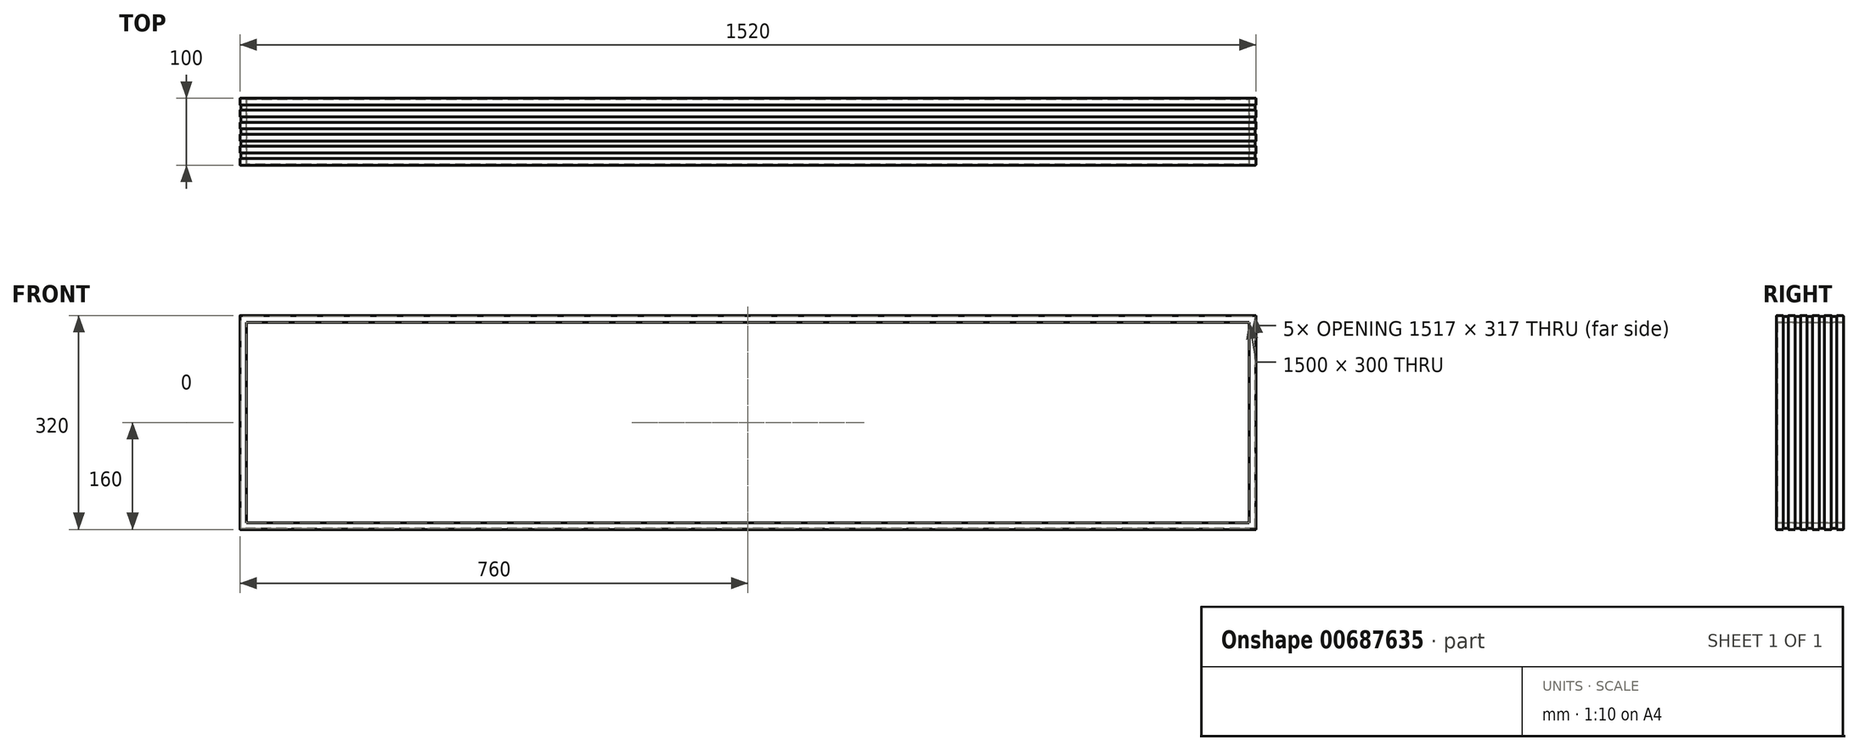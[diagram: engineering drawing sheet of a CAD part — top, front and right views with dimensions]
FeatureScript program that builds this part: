
annotation { "Feature Type Name" : "Feature", "Feature Type Description" : "" }
export const myFeature = defineFeature(function(context is Context, id is Id, definition is map)
    precondition{}
    {
        {
            var Q0;
            Q0=qCreatedBy(makeId("Front.planeOp"),FACE);
            var sketch = newSketch(context, id + "F0", { "sketchPlane" : qUnion([Q0])});
            skLineSegment(sketch, "E0.bottom", {"start": v(-1550, 0) * mm, "end": v(-1500, 0) * mm});
            skLineSegment(sketch, "E0.top", {"start": v(-1550, -2720) * mm, "end": v(-1500, -2720) * mm});
            skLineSegment(sketch, "E0.left", {"start": v(-1550, 0) * mm, "end": v(-1550, -2720) * mm});
            skLineSegment(sketch, "E0.right", {"start": v(-1500, 0) * mm, "end": v(-1500, -2720) * mm});
            skLineSegment(sketch, "E1.MirrorCS", {"start": v(1550, -2720) * mm, "end": v(1500, -2720) * mm});
            skLineSegment(sketch, "E2.MirrorCS", {"start": v(1500, 0) * mm, "end": v(1500, -2720) * mm});
            skLineSegment(sketch, "E3.MirrorCS", {"start": v(1550, 0) * mm, "end": v(1500, 0) * mm});
            skLineSegment(sketch, "E4.MirrorCS", {"start": v(1550, 0) * mm, "end": v(1550, -2720) * mm});
            skSolve(sketch);
        }
        {
            var Q0;
            Q0=qSketchRegion(id+"F0",true);
            extrude(context, id + "F1", {"entities" : qUnion([Q0]), "depth" : 100 * mm, "offsetDistance" : 25 * mm});
        }
        {
            var Q0;
            Q0=makeQuery(id+"F1.opExtrude","SWEPT_FACE",FACE,{"disambiguationData":[OSD([sQuery(id+"F0.wireOp",EDGE,"E0.bottom")])]});
            var sketch = newSketch(context, id + "F2", { "sketchPlane" : qUnion([Q0])});
            skLineSegment(sketch, "E5.bottom", {"start": v(-1550, -100) * mm, "end": v(-3070, -100) * mm});
            skLineSegment(sketch, "E5.top", {"start": v(-1550, 0) * mm, "end": v(-3070, 0) * mm});
            skLineSegment(sketch, "E5.left", {"start": v(-1550, -100) * mm, "end": v(-1550, 0) * mm});
            skLineSegment(sketch, "E5.right", {"start": v(-3070, -100) * mm, "end": v(-3070, 0) * mm});
            skLineSegment(sketch, "E6.bottom", {"start": v(-1500, -100) * mm, "end": v(1500, -100) * mm});
            skLineSegment(sketch, "E6.top", {"start": v(-1500, 0) * mm, "end": v(1500, 0) * mm});
            skLineSegment(sketch, "E6.left", {"start": v(-1500, -100) * mm, "end": v(-1500, 0) * mm});
            skLineSegment(sketch, "E6.right", {"start": v(1500, -100) * mm, "end": v(1500, 0) * mm});
            skLineSegment(sketch, "E7.bottom", {"start": v(1550, -100) * mm, "end": v(2770, -100) * mm});
            skLineSegment(sketch, "E7.top", {"start": v(1550, 0) * mm, "end": v(2770, 0) * mm});
            skLineSegment(sketch, "E7.left", {"start": v(1550, -100) * mm, "end": v(1550, 0) * mm});
            skLineSegment(sketch, "E7.right", {"start": v(2770, -100) * mm, "end": v(2770, 0) * mm});
            skSolve(sketch);
        }
        {
            var Q0;
            Q0=qSketchRegion(id+"F2",true);
            extrude(context, id + "F3", {"entities" : qUnion([Q0]), "oppositeDirection" : true, "depth" : 320 * mm, "offsetDistance" : 25 * mm});
        }
        {
            var Q0;
            Q0=makeQuery(id+"F3.opExtrude","SWEPT_FACE",FACE,{"disambiguationData":[OSD([sQuery(id+"F2.wireOp",EDGE,"E6.bottom")])]});
            var sketch = newSketch(context, id + "F4", { "sketchPlane" : qUnion([Q0])});
            skLineSegment(sketch, "E8.0", {"start": v(-1560, -10) * mm, "end": v(-3060, -10) * mm});
            skLineSegment(sketch, "E8.1", {"start": v(-1560, -310) * mm, "end": v(-1560, -10) * mm});
            skLineSegment(sketch, "E8.2", {"start": v(-3060, -310) * mm, "end": v(-1560, -310) * mm});
            skLineSegment(sketch, "E8.3", {"start": v(-3060, -10) * mm, "end": v(-3060, -310) * mm});
            skLineSegment(sketch, "E9.0", {"start": v(1490, -10) * mm, "end": v(-1490, -10) * mm});
            skLineSegment(sketch, "E9.1", {"start": v(1490, -310) * mm, "end": v(1490, -10) * mm});
            skLineSegment(sketch, "E9.2", {"start": v(-1490, -310) * mm, "end": v(1490, -310) * mm});
            skLineSegment(sketch, "E9.3", {"start": v(-1490, -10) * mm, "end": v(-1490, -310) * mm});
            skLineSegment(sketch, "E10.0", {"start": v(2760, -10) * mm, "end": v(1560, -10) * mm});
            skLineSegment(sketch, "E10.1", {"start": v(2760, -310) * mm, "end": v(2760, -10) * mm});
            skLineSegment(sketch, "E10.2", {"start": v(1560, -310) * mm, "end": v(2760, -310) * mm});
            skLineSegment(sketch, "E10.3", {"start": v(1560, -10) * mm, "end": v(1560, -310) * mm});
            skSolve(sketch);
        }
        {
            var Q0;
            Q0=qSketchRegion(id+"F4",true);
            extrude(context, id + "F5", {"entities" : qUnion([Q0]), "operationType" : NewBodyOperationType.REMOVE, "endBound" : BoundingType.THROUGH_ALL, "oppositeDirection" : true, "depth" : 25 * mm, "offsetDistance" : 25 * mm});
        }
        {
            var Q0;
            Q0=makeQuery(id+"F3.opExtrude","SWEPT_FACE",FACE,{"disambiguationData":[OSD([sQuery(id+"F2.wireOp",EDGE,"E5.right")])]});
            var sketch = newSketch(context, id + "F6", { "sketchPlane" : qUnion([Q0])});
            skLineSegment(sketch, "E11", {"start": v(10, 0) * mm, "end": v(10, -1.5) * mm});
            skLineSegment(sketch, "E12", {"start": v(10, -1.5) * mm, "end": v(18, -1.5) * mm});
            skLineSegment(sketch, "E13", {"start": v(18, -1.5) * mm, "end": v(18, 0) * mm});
            skLineSegment(sketch, "E14.1.0.0", {"start": v(36, -1.5) * mm, "end": v(36, 0) * mm});
            skLineSegment(sketch, "E14.1.0.1", {"start": v(28, -1.5) * mm, "end": v(36, -1.5) * mm});
            skLineSegment(sketch, "E14.1.0.2", {"start": v(28, 0) * mm, "end": v(28, -1.5) * mm});
            skLineSegment(sketch, "E14.2.0.0", {"start": v(54, -1.5) * mm, "end": v(54, 0) * mm});
            skLineSegment(sketch, "E14.2.0.1", {"start": v(46, -1.5) * mm, "end": v(54, -1.5) * mm});
            skLineSegment(sketch, "E14.2.0.2", {"start": v(46, 0) * mm, "end": v(46, -1.5) * mm});
            skLineSegment(sketch, "E14.3.0.0", {"start": v(72, -1.5) * mm, "end": v(72, 0) * mm});
            skLineSegment(sketch, "E14.3.0.1", {"start": v(64, -1.5) * mm, "end": v(72, -1.5) * mm});
            skLineSegment(sketch, "E14.3.0.2", {"start": v(64, 0) * mm, "end": v(64, -1.5) * mm});
            skLineSegment(sketch, "E14.4.0.0", {"start": v(90, -1.5) * mm, "end": v(90, 0) * mm});
            skLineSegment(sketch, "E14.4.0.1", {"start": v(82, -1.5) * mm, "end": v(90, -1.5) * mm});
            skLineSegment(sketch, "E14.4.0.2", {"start": v(82, 0) * mm, "end": v(82, -1.5) * mm});
            skLineSegment(sketch, "E14.direction1", {"start": v(10, -1.5) * mm, "end": v(28, -1.5) * mm, "construction": true});
            skLineSegment(sketch, "E15", {"start": v(10, 0) * mm, "end": v(18, 0) * mm});
            skLineSegment(sketch, "E16", {"start": v(28, 0) * mm, "end": v(36, 0) * mm});
            skLineSegment(sketch, "E17", {"start": v(46, 0) * mm, "end": v(54, 0) * mm});
            skLineSegment(sketch, "E18", {"start": v(64, 0) * mm, "end": v(72, 0) * mm});
            skLineSegment(sketch, "E19", {"start": v(82, 0) * mm, "end": v(90, 0) * mm});
            skLineSegment(sketch, "E20", {"start": v(100, -160) * mm, "end": v(0, -160) * mm, "construction": true});
            skLineSegment(sketch, "E21.MirrorCS", {"start": v(90, -318.5) * mm, "end": v(90, -320) * mm});
            skLineSegment(sketch, "E22.MirrorCS", {"start": v(64, -320) * mm, "end": v(64, -318.5) * mm});
            skLineSegment(sketch, "E23.MirrorCS", {"start": v(10, -320) * mm, "end": v(10, -318.5) * mm});
            skLineSegment(sketch, "E24.MirrorCS", {"start": v(18, -318.5) * mm, "end": v(18, -320) * mm});
            skLineSegment(sketch, "E25.MirrorCS", {"start": v(36, -318.5) * mm, "end": v(36, -320) * mm});
            skLineSegment(sketch, "E26.MirrorCS", {"start": v(28, -320) * mm, "end": v(28, -318.5) * mm});
            skLineSegment(sketch, "E27.MirrorCS", {"start": v(54, -318.5) * mm, "end": v(54, -320) * mm});
            skLineSegment(sketch, "E28.MirrorCS", {"start": v(46, -320) * mm, "end": v(46, -318.5) * mm});
            skLineSegment(sketch, "E29.MirrorCS", {"start": v(72, -318.5) * mm, "end": v(72, -320) * mm});
            skLineSegment(sketch, "E30.MirrorCS", {"start": v(82, -320) * mm, "end": v(82, -318.5) * mm});
            skLineSegment(sketch, "E31.MirrorCS", {"start": v(10, -320) * mm, "end": v(18, -320) * mm});
            skLineSegment(sketch, "E32.MirrorCS", {"start": v(10, -318.5) * mm, "end": v(18, -318.5) * mm});
            skLineSegment(sketch, "E33.MirrorCS", {"start": v(64, -318.5) * mm, "end": v(72, -318.5) * mm});
            skLineSegment(sketch, "E34.MirrorCS", {"start": v(64, -320) * mm, "end": v(72, -320) * mm});
            skLineSegment(sketch, "E35.MirrorCS", {"start": v(82, -320) * mm, "end": v(90, -320) * mm});
            skLineSegment(sketch, "E36.MirrorCS", {"start": v(28, -320) * mm, "end": v(36, -320) * mm});
            skLineSegment(sketch, "E37.MirrorCS", {"start": v(82, -318.5) * mm, "end": v(90, -318.5) * mm});
            skLineSegment(sketch, "E38.MirrorCS", {"start": v(10, -318.5) * mm, "end": v(28, -318.5) * mm, "construction": true});
            skLineSegment(sketch, "E39.MirrorCS", {"start": v(46, -320) * mm, "end": v(54, -320) * mm});
            skLineSegment(sketch, "E40.MirrorCS", {"start": v(28, -318.5) * mm, "end": v(36, -318.5) * mm});
            skLineSegment(sketch, "E41.MirrorCS", {"start": v(46, -318.5) * mm, "end": v(54, -318.5) * mm});
            skSolve(sketch);
        }
        {
            var Q0;
            Q0=qSketchRegion(id+"F6",true);
            extrude(context, id + "F7", {"entities" : qUnion([Q0]), "operationType" : NewBodyOperationType.REMOVE, "endBound" : BoundingType.THROUGH_ALL, "oppositeDirection" : true, "depth" : 25 * mm, "offsetDistance" : 25 * mm});
        }
        {
            var Q0;
            {var subQ0=sQuery(id+"F2.wireOp",EDGE,"E5.top");var subQ1=sQuery(id+"F2.wireOp",EDGE,"E5.left");var subQ2=sQuery(id+"F2.wireOp",EDGE,"E5.right");Q0=makeQuery(id+"F7.boolean.opBoolean","SPLIT",FACE,{"disambiguationData":[TD([makeQuery(id+"F3.opExtrude","SWEPT_FACE",FACE,{"disambiguationData":[OSD([subQ0])]})])],"derivedFrom":makeQuery(id+"F3.opExtrude","CAP_FACE",FACE,{"disambiguationData":[OSD([sQuery(id+"F2.wireOp",EDGE,"E5.bottom"),subQ0,subQ1,subQ2])],"isStart":true})});}
            var sketch = newSketch(context, id + "F8", { "sketchPlane" : qUnion([Q0])});
            skLineSegment(sketch, "E42.bottom", {"start": v(-3068.5, -90) * mm, "end": v(-3070, -90) * mm});
            skLineSegment(sketch, "E42.top", {"start": v(-3068.5, -82) * mm, "end": v(-3070, -82) * mm});
            skLineSegment(sketch, "E42.left", {"start": v(-3068.5, -90) * mm, "end": v(-3068.5, -82) * mm});
            skLineSegment(sketch, "E42.right", {"start": v(-3070, -90) * mm, "end": v(-3070, -82) * mm});
            skLineSegment(sketch, "E43.0.1.0", {"start": v(-3068.5, -64) * mm, "end": v(-3070, -64) * mm});
            skLineSegment(sketch, "E43.0.1.1", {"start": v(-3068.5, -72) * mm, "end": v(-3070, -72) * mm});
            skLineSegment(sketch, "E43.0.1.2", {"start": v(-3070, -72) * mm, "end": v(-3070, -64) * mm});
            skLineSegment(sketch, "E43.0.1.3", {"start": v(-3068.5, -72) * mm, "end": v(-3068.5, -64) * mm});
            skLineSegment(sketch, "E43.0.2.0", {"start": v(-3068.5, -46) * mm, "end": v(-3070, -46) * mm});
            skLineSegment(sketch, "E43.0.2.1", {"start": v(-3068.5, -54) * mm, "end": v(-3070, -54) * mm});
            skLineSegment(sketch, "E43.0.2.2", {"start": v(-3070, -54) * mm, "end": v(-3070, -46) * mm});
            skLineSegment(sketch, "E43.0.2.3", {"start": v(-3068.5, -54) * mm, "end": v(-3068.5, -46) * mm});
            skLineSegment(sketch, "E43.0.3.0", {"start": v(-3068.5, -28) * mm, "end": v(-3070, -28) * mm});
            skLineSegment(sketch, "E43.0.3.1", {"start": v(-3068.5, -36) * mm, "end": v(-3070, -36) * mm});
            skLineSegment(sketch, "E43.0.3.2", {"start": v(-3070, -36) * mm, "end": v(-3070, -28) * mm});
            skLineSegment(sketch, "E43.0.3.3", {"start": v(-3068.5, -36) * mm, "end": v(-3068.5, -28) * mm});
            skLineSegment(sketch, "E43.0.4.0", {"start": v(-3068.5, -10) * mm, "end": v(-3070, -10) * mm});
            skLineSegment(sketch, "E43.0.4.1", {"start": v(-3068.5, -18) * mm, "end": v(-3070, -18) * mm});
            skLineSegment(sketch, "E43.0.4.2", {"start": v(-3070, -18) * mm, "end": v(-3070, -10) * mm});
            skLineSegment(sketch, "E43.0.4.3", {"start": v(-3068.5, -18) * mm, "end": v(-3068.5, -10) * mm});
            skLineSegment(sketch, "E43.direction1", {"start": v(-3070, -90) * mm, "end": v(-2770, -90) * mm, "construction": true});
            skLineSegment(sketch, "E43.direction2", {"start": v(-3070, -90) * mm, "end": v(-3070, -72) * mm, "construction": true});
            skPoint(sketch, "E44.0", {"position": v(0, -10) * mm});
            skLineSegment(sketch, "E45.MirrorCS", {"start": v(3068.5, -64) * mm, "end": v(3070, -64) * mm});
            skLineSegment(sketch, "E46.MirrorCS", {"start": v(3068.5, -36) * mm, "end": v(3070, -36) * mm});
            skLineSegment(sketch, "E47.MirrorCS", {"start": v(3068.5, -90) * mm, "end": v(3070, -90) * mm});
            skLineSegment(sketch, "E48.MirrorCS", {"start": v(3068.5, -82) * mm, "end": v(3070, -82) * mm});
            skLineSegment(sketch, "E49.MirrorCS", {"start": v(3068.5, -72) * mm, "end": v(3070, -72) * mm});
            skLineSegment(sketch, "E50.MirrorCS", {"start": v(3068.5, -46) * mm, "end": v(3070, -46) * mm});
            skLineSegment(sketch, "E51.MirrorCS", {"start": v(3068.5, -54) * mm, "end": v(3070, -54) * mm});
            skLineSegment(sketch, "E52.MirrorCS", {"start": v(3070, -36) * mm, "end": v(3070, -28) * mm});
            skLineSegment(sketch, "E53.MirrorCS", {"start": v(3068.5, -90) * mm, "end": v(3068.5, -82) * mm});
            skLineSegment(sketch, "E54.MirrorCS", {"start": v(3070, -72) * mm, "end": v(3070, -64) * mm});
            skLineSegment(sketch, "E55.MirrorCS", {"start": v(3070, -54) * mm, "end": v(3070, -46) * mm});
            skLineSegment(sketch, "E56.MirrorCS", {"start": v(3068.5, -36) * mm, "end": v(3068.5, -28) * mm});
            skLineSegment(sketch, "E57.MirrorCS", {"start": v(3070, -90) * mm, "end": v(3070, -82) * mm});
            skLineSegment(sketch, "E58.MirrorCS", {"start": v(3068.5, -72) * mm, "end": v(3068.5, -64) * mm});
            skLineSegment(sketch, "E59.MirrorCS", {"start": v(3068.5, -54) * mm, "end": v(3068.5, -46) * mm});
            skLineSegment(sketch, "E60.MirrorCS", {"start": v(3068.5, -28) * mm, "end": v(3070, -28) * mm});
            skLineSegment(sketch, "E61.MirrorCS", {"start": v(3070, -90) * mm, "end": v(3070, -72) * mm, "construction": true});
            skLineSegment(sketch, "E62.MirrorCS", {"start": v(3070, -90) * mm, "end": v(2770, -90) * mm, "construction": true});
            skLineSegment(sketch, "E63.MirrorCS", {"start": v(3068.5, -18) * mm, "end": v(3070, -18) * mm});
            skLineSegment(sketch, "E64.MirrorCS", {"start": v(3070, -18) * mm, "end": v(3070, -10) * mm});
            skLineSegment(sketch, "E65.MirrorCS", {"start": v(3068.5, -18) * mm, "end": v(3068.5, -10) * mm});
            skLineSegment(sketch, "E66.MirrorCS", {"start": v(3068.5, -10) * mm, "end": v(3070, -10) * mm});
            skLineSegment(sketch, "E67", {"start": v(-2310, 0) * mm, "end": v(-2310, -98.65) * mm, "construction": true});
            skLineSegment(sketch, "E68.MirrorCS", {"start": v(-1551.5, -90) * mm, "end": v(-1550, -90) * mm});
            skLineSegment(sketch, "E69.MirrorCS", {"start": v(-1551.5, -72) * mm, "end": v(-1550, -72) * mm});
            skLineSegment(sketch, "E70.MirrorCS", {"start": v(-1551.5, -46) * mm, "end": v(-1550, -46) * mm});
            skLineSegment(sketch, "E71.MirrorCS", {"start": v(-1551.5, -28) * mm, "end": v(-1550, -28) * mm});
            skLineSegment(sketch, "E72.MirrorCS", {"start": v(-1551.5, -36) * mm, "end": v(-1550, -36) * mm});
            skLineSegment(sketch, "E73.MirrorCS", {"start": v(-1551.5, -10) * mm, "end": v(-1550, -10) * mm});
            skLineSegment(sketch, "E74.MirrorCS", {"start": v(-1551.5, -64) * mm, "end": v(-1550, -64) * mm});
            skLineSegment(sketch, "E75.MirrorCS", {"start": v(-1551.5, -54) * mm, "end": v(-1550, -54) * mm});
            skLineSegment(sketch, "E76.MirrorCS", {"start": v(-1551.5, -18) * mm, "end": v(-1550, -18) * mm});
            skLineSegment(sketch, "E77.MirrorCS", {"start": v(-1551.5, -82) * mm, "end": v(-1550, -82) * mm});
            skLineSegment(sketch, "E78.MirrorCS", {"start": v(-1550, -90) * mm, "end": v(-1550, -82) * mm});
            skLineSegment(sketch, "E79.MirrorCS", {"start": v(-1550, -72) * mm, "end": v(-1550, -64) * mm});
            skLineSegment(sketch, "E80.MirrorCS", {"start": v(-1551.5, -72) * mm, "end": v(-1551.5, -64) * mm});
            skLineSegment(sketch, "E81.MirrorCS", {"start": v(-1551.5, -36) * mm, "end": v(-1551.5, -28) * mm});
            skLineSegment(sketch, "E82.MirrorCS", {"start": v(-1550, -90) * mm, "end": v(-1550, -72) * mm, "construction": true});
            skLineSegment(sketch, "E83.MirrorCS", {"start": v(-1550, -18) * mm, "end": v(-1550, -10) * mm});
            skLineSegment(sketch, "E84.MirrorCS", {"start": v(-1550, -90) * mm, "end": v(-1850, -90) * mm, "construction": true});
            skLineSegment(sketch, "E85.MirrorCS", {"start": v(-1550, -54) * mm, "end": v(-1550, -46) * mm});
            skLineSegment(sketch, "E86.MirrorCS", {"start": v(-1551.5, -54) * mm, "end": v(-1551.5, -46) * mm});
            skLineSegment(sketch, "E87.MirrorCS", {"start": v(-1551.5, -90) * mm, "end": v(-1551.5, -82) * mm});
            skLineSegment(sketch, "E88.MirrorCS", {"start": v(-1550, -36) * mm, "end": v(-1550, -28) * mm});
            skLineSegment(sketch, "E89.MirrorCS", {"start": v(-1551.5, -18) * mm, "end": v(-1551.5, -10) * mm});
            skSolve(sketch);
        }
        {
            var Q0;
            Q0=qSketchRegion(id+"F8",true);
            extrude(context, id + "F9", {"entities" : qUnion([Q0]), "operationType" : NewBodyOperationType.REMOVE, "endBound" : BoundingType.THROUGH_ALL, "oppositeDirection" : true, "depth" : 25 * mm, "offsetDistance" : 25 * mm});
        }
        {
            var Q0;
            Q0=makeQuery(id+"F3.opExtrude","SWEPT_FACE",FACE,{"disambiguationData":[OSD([sQuery(id+"F2.wireOp",EDGE,"E7.top")])]});
            cPlane(context, id + "F10", {"entities" : qUnion([Q0]), "cplaneType" : CPlaneType.OFFSET, "offset" : 1 * mm, "oppositeDirection" : true, "width" : 150 * mm, "height" : 150 * mm});
        }
        {
            var Q0;
            Q0=qCreatedBy(id+"F10.planeOp",FACE);
            var sketch = newSketch(context, id + "F11", { "sketchPlane" : qUnion([Q0])});
            skLineSegment(sketch, "E90.0", {"start": v(1490, -10) * mm, "end": v(1490, -310) * mm});
            skLineSegment(sketch, "E90.1", {"start": v(-1490, -10) * mm, "end": v(1490, -10) * mm});
            skLineSegment(sketch, "E90.2", {"start": v(1490, -310) * mm, "end": v(-1490, -310) * mm});
            skLineSegment(sketch, "E90.3", {"start": v(-1490, -310) * mm, "end": v(-1490, -10) * mm});
            skLineSegment(sketch, "E90.4", {"start": v(-1560, -10) * mm, "end": v(-1560, -310) * mm});
            skLineSegment(sketch, "E90.5", {"start": v(-1560, -310) * mm, "end": v(-2760, -310) * mm});
            skLineSegment(sketch, "E90.6", {"start": v(-2760, -10) * mm, "end": v(-1560, -10) * mm});
            skLineSegment(sketch, "E90.7", {"start": v(-2760, -310) * mm, "end": v(-2760, -10) * mm});
            skLineSegment(sketch, "E90.8", {"start": v(1560, -10) * mm, "end": v(1560, -310) * mm});
            skLineSegment(sketch, "E90.9", {"start": v(1560, -310) * mm, "end": v(3060, -310) * mm});
            skLineSegment(sketch, "E90.10", {"start": v(3060, -10) * mm, "end": v(1560, -10) * mm});
            skLineSegment(sketch, "E90.11", {"start": v(3060, -310) * mm, "end": v(3060, -10) * mm});
            skSolve(sketch);
        }
        {
            var Q0;
            Q0=qSketchRegion(id+"F11",true);
            var Q1;
            Q1=makeQuery(id+"F3.opExtrude","SWEPT_FACE",FACE,{"disambiguationData":[OSD([sQuery(id+"F2.wireOp",EDGE,"E5.bottom")])]});
            extrude(context, id + "F12", {"entities" : qUnion([Q0]), "endBound" : BoundingType.UP_TO_SURFACE, "oppositeDirection" : true, "depth" : 25 * mm, "endBoundEntityFace" : qUnion([Q1]), "hasOffset" : true, "offsetDistance" : 1 * mm});
        }
        {
            var Q0;
            {var subQ0=sQuery(id+"F2.wireOp",EDGE,"E7.right");var subQ1=sQuery(id+"F2.wireOp",EDGE,"E7.top");Q0=makeQuery(id+"F7.boolean.opBoolean","SPLIT",EDGE,{"disambiguationData":[TD([makeQuery(id+"F3.opExtrude","SWEPT_FACE",FACE,{"disambiguationData":[OSD([subQ1])]})])],"derivedFrom":makeQuery(id+"F3.opExtrude","CAP_EDGE",EDGE,{"disambiguationData":[OSD([subQ0])],"isStart":true})});}
            var Q1;
            {var subQ0=sQuery(id+"F2.wireOp",EDGE,"E7.right");Q1=makeQuery(id+"F7.boolean.opBoolean","SPLIT",EDGE,{"disambiguationData":[TD([makeQuery(id+"F7.opExtrude","SWEPT_FACE",FACE,{"disambiguationData":[OSD([sQuery(id+"F6.wireOp",EDGE,"E13")])]})])],"derivedFrom":makeQuery(id+"F3.opExtrude","CAP_EDGE",EDGE,{"disambiguationData":[OSD([subQ0])],"isStart":true})});}
            var Q2;
            {var subQ0=sQuery(id+"F2.wireOp",EDGE,"E7.right");Q2=makeQuery(id+"F7.boolean.opBoolean","SPLIT",EDGE,{"disambiguationData":[TD([makeQuery(id+"F7.opExtrude","SWEPT_FACE",FACE,{"disambiguationData":[OSD([sQuery(id+"F6.wireOp",EDGE,"E14.1.0.0")])]})])],"derivedFrom":makeQuery(id+"F3.opExtrude","CAP_EDGE",EDGE,{"disambiguationData":[OSD([subQ0])],"isStart":true})});}
            var Q3;
            {var subQ0=sQuery(id+"F2.wireOp",EDGE,"E7.right");Q3=makeQuery(id+"F7.boolean.opBoolean","SPLIT",EDGE,{"disambiguationData":[TD([makeQuery(id+"F7.opExtrude","SWEPT_FACE",FACE,{"disambiguationData":[OSD([sQuery(id+"F6.wireOp",EDGE,"E14.2.0.0")])]})])],"derivedFrom":makeQuery(id+"F3.opExtrude","CAP_EDGE",EDGE,{"disambiguationData":[OSD([subQ0])],"isStart":true})});}
            var Q4;
            {var subQ0=sQuery(id+"F2.wireOp",EDGE,"E7.right");Q4=makeQuery(id+"F7.boolean.opBoolean","SPLIT",EDGE,{"disambiguationData":[TD([makeQuery(id+"F7.opExtrude","SWEPT_FACE",FACE,{"disambiguationData":[OSD([sQuery(id+"F6.wireOp",EDGE,"E14.3.0.0")])]})])],"derivedFrom":makeQuery(id+"F3.opExtrude","CAP_EDGE",EDGE,{"disambiguationData":[OSD([subQ0])],"isStart":true})});}
            var Q5;
            {var subQ0=sQuery(id+"F2.wireOp",EDGE,"E7.bottom");var subQ1=sQuery(id+"F2.wireOp",EDGE,"E7.right");Q5=makeQuery(id+"F7.boolean.opBoolean","SPLIT",EDGE,{"disambiguationData":[TD([makeQuery(id+"F3.opExtrude","SWEPT_FACE",FACE,{"disambiguationData":[OSD([subQ0])]})])],"derivedFrom":makeQuery(id+"F3.opExtrude","CAP_EDGE",EDGE,{"disambiguationData":[OSD([subQ1])],"isStart":true})});}
            var Q6;
            Q6=makeQuery(id+"F9.boolean.opBoolean","INTERSECT",EDGE,{"derivedFrom":[makeQuery(id+"F7.boolean.opBoolean","COPY",FACE,{"disambiguationData":[TD([makeQuery(id+"F3.opExtrude","SWEPT_FACE",FACE,{"disambiguationData":[OSD([sQuery(id+"F2.wireOp",EDGE,"E7.left")])]})])],"derivedFrom":makeQuery(id+"F7.opExtrude","SWEPT_FACE",FACE,{"disambiguationData":[OSD([sQuery(id+"F6.wireOp",EDGE,"E14.4.0.1")])]})}),makeQuery(id+"F9.opExtrude","SWEPT_FACE",FACE,{"disambiguationData":[OSD([sQuery(id+"F8.wireOp",EDGE,"E53.MirrorCS")])]})]});
            var Q7;
            Q7=makeQuery(id+"F9.boolean.opBoolean","INTERSECT",EDGE,{"derivedFrom":[makeQuery(id+"F7.boolean.opBoolean","COPY",FACE,{"disambiguationData":[TD([makeQuery(id+"F3.opExtrude","SWEPT_FACE",FACE,{"disambiguationData":[OSD([sQuery(id+"F2.wireOp",EDGE,"E7.left")])]})])],"derivedFrom":makeQuery(id+"F7.opExtrude","SWEPT_FACE",FACE,{"disambiguationData":[OSD([sQuery(id+"F6.wireOp",EDGE,"E14.3.0.1")])]})}),makeQuery(id+"F9.opExtrude","SWEPT_FACE",FACE,{"disambiguationData":[OSD([sQuery(id+"F8.wireOp",EDGE,"E58.MirrorCS")])]})]});
            var Q8;
            Q8=makeQuery(id+"F9.boolean.opBoolean","INTERSECT",EDGE,{"derivedFrom":[makeQuery(id+"F7.boolean.opBoolean","COPY",FACE,{"disambiguationData":[TD([makeQuery(id+"F3.opExtrude","SWEPT_FACE",FACE,{"disambiguationData":[OSD([sQuery(id+"F2.wireOp",EDGE,"E7.left")])]})])],"derivedFrom":makeQuery(id+"F7.opExtrude","SWEPT_FACE",FACE,{"disambiguationData":[OSD([sQuery(id+"F6.wireOp",EDGE,"E14.2.0.1")])]})}),makeQuery(id+"F9.opExtrude","SWEPT_FACE",FACE,{"disambiguationData":[OSD([sQuery(id+"F8.wireOp",EDGE,"E59.MirrorCS")])]})]});
            var Q9;
            Q9=makeQuery(id+"F9.boolean.opBoolean","INTERSECT",EDGE,{"derivedFrom":[makeQuery(id+"F7.boolean.opBoolean","COPY",FACE,{"disambiguationData":[TD([makeQuery(id+"F3.opExtrude","SWEPT_FACE",FACE,{"disambiguationData":[OSD([sQuery(id+"F2.wireOp",EDGE,"E7.left")])]})])],"derivedFrom":makeQuery(id+"F7.opExtrude","SWEPT_FACE",FACE,{"disambiguationData":[OSD([sQuery(id+"F6.wireOp",EDGE,"E14.1.0.1")])]})}),makeQuery(id+"F9.opExtrude","SWEPT_FACE",FACE,{"disambiguationData":[OSD([sQuery(id+"F8.wireOp",EDGE,"E56.MirrorCS")])]})]});
            var Q10;
            Q10=makeQuery(id+"F9.boolean.opBoolean","INTERSECT",EDGE,{"derivedFrom":[makeQuery(id+"F7.boolean.opBoolean","COPY",FACE,{"disambiguationData":[TD([makeQuery(id+"F3.opExtrude","SWEPT_FACE",FACE,{"disambiguationData":[OSD([sQuery(id+"F2.wireOp",EDGE,"E7.left")])]})])],"derivedFrom":makeQuery(id+"F7.opExtrude","SWEPT_FACE",FACE,{"disambiguationData":[OSD([sQuery(id+"F6.wireOp",EDGE,"E12")])]})}),makeQuery(id+"F9.opExtrude","SWEPT_FACE",FACE,{"disambiguationData":[OSD([sQuery(id+"F8.wireOp",EDGE,"E65.MirrorCS")])]})]});
            var Q11;
            {var subQ0=sQuery(id+"F2.wireOp",EDGE,"E7.left");var subQ1=sQuery(id+"F2.wireOp",EDGE,"E7.top");Q11=makeQuery(id+"F7.boolean.opBoolean","SPLIT",EDGE,{"disambiguationData":[TD([makeQuery(id+"F3.opExtrude","SWEPT_FACE",FACE,{"disambiguationData":[OSD([subQ1])]})])],"derivedFrom":makeQuery(id+"F3.opExtrude","CAP_EDGE",EDGE,{"disambiguationData":[OSD([subQ0])],"isStart":true})});}
            var Q12;
            {var subQ0=sQuery(id+"F2.wireOp",EDGE,"E7.left");Q12=makeQuery(id+"F7.boolean.opBoolean","SPLIT",EDGE,{"disambiguationData":[TD([makeQuery(id+"F7.opExtrude","SWEPT_FACE",FACE,{"disambiguationData":[OSD([sQuery(id+"F6.wireOp",EDGE,"E13")])]})])],"derivedFrom":makeQuery(id+"F3.opExtrude","CAP_EDGE",EDGE,{"disambiguationData":[OSD([subQ0])],"isStart":true})});}
            var Q13;
            {var subQ0=sQuery(id+"F2.wireOp",EDGE,"E7.left");Q13=makeQuery(id+"F7.boolean.opBoolean","SPLIT",EDGE,{"disambiguationData":[TD([makeQuery(id+"F7.opExtrude","SWEPT_FACE",FACE,{"disambiguationData":[OSD([sQuery(id+"F6.wireOp",EDGE,"E14.1.0.0")])]})])],"derivedFrom":makeQuery(id+"F3.opExtrude","CAP_EDGE",EDGE,{"disambiguationData":[OSD([subQ0])],"isStart":true})});}
            var Q14;
            {var subQ0=sQuery(id+"F2.wireOp",EDGE,"E7.left");Q14=makeQuery(id+"F7.boolean.opBoolean","SPLIT",EDGE,{"disambiguationData":[TD([makeQuery(id+"F7.opExtrude","SWEPT_FACE",FACE,{"disambiguationData":[OSD([sQuery(id+"F6.wireOp",EDGE,"E14.2.0.0")])]})])],"derivedFrom":makeQuery(id+"F3.opExtrude","CAP_EDGE",EDGE,{"disambiguationData":[OSD([subQ0])],"isStart":true})});}
            var Q15;
            {var subQ0=sQuery(id+"F2.wireOp",EDGE,"E7.bottom");var subQ1=sQuery(id+"F2.wireOp",EDGE,"E7.left");Q15=makeQuery(id+"F7.boolean.opBoolean","SPLIT",EDGE,{"disambiguationData":[TD([makeQuery(id+"F3.opExtrude","SWEPT_FACE",FACE,{"disambiguationData":[OSD([subQ0])]})])],"derivedFrom":makeQuery(id+"F3.opExtrude","CAP_EDGE",EDGE,{"disambiguationData":[OSD([subQ1])],"isStart":true})});}
            var Q16;
            Q16=makeQuery(id+"F1.opExtrude","SWEPT_EDGE",EDGE,{"disambiguationData":[OSD([sQuery(id+"F0.wireOp",EDGE,"E3.MirrorCS"),sQuery(id+"F0.wireOp",EDGE,"E4.MirrorCS")])]});
            var Q17;
            {var subQ0=sQuery(id+"F2.wireOp",EDGE,"E7.left");Q17=makeQuery(id+"F7.boolean.opBoolean","SPLIT",EDGE,{"disambiguationData":[TD([makeQuery(id+"F7.opExtrude","SWEPT_FACE",FACE,{"disambiguationData":[OSD([sQuery(id+"F6.wireOp",EDGE,"E14.3.0.0")])]})])],"derivedFrom":makeQuery(id+"F3.opExtrude","CAP_EDGE",EDGE,{"disambiguationData":[OSD([subQ0])],"isStart":true})});}
            var Q18;
            Q18=makeQuery(id+"F7.boolean.opBoolean","INTERSECT",EDGE,{"derivedFrom":[makeQuery(id+"F3.opExtrude","SWEPT_FACE",FACE,{"disambiguationData":[OSD([sQuery(id+"F2.wireOp",EDGE,"E7.left")])]}),makeQuery(id+"F7.opExtrude","SWEPT_FACE",FACE,{"disambiguationData":[OSD([sQuery(id+"F6.wireOp",EDGE,"E14.4.0.1")])]})]});
            var Q19;
            Q19=makeQuery(id+"F7.boolean.opBoolean","INTERSECT",EDGE,{"derivedFrom":[makeQuery(id+"F3.opExtrude","SWEPT_FACE",FACE,{"disambiguationData":[OSD([sQuery(id+"F2.wireOp",EDGE,"E7.left")])]}),makeQuery(id+"F7.opExtrude","SWEPT_FACE",FACE,{"disambiguationData":[OSD([sQuery(id+"F6.wireOp",EDGE,"E14.3.0.1")])]})]});
            var Q20;
            Q20=makeQuery(id+"F7.boolean.opBoolean","INTERSECT",EDGE,{"derivedFrom":[makeQuery(id+"F3.opExtrude","SWEPT_FACE",FACE,{"disambiguationData":[OSD([sQuery(id+"F2.wireOp",EDGE,"E7.left")])]}),makeQuery(id+"F7.opExtrude","SWEPT_FACE",FACE,{"disambiguationData":[OSD([sQuery(id+"F6.wireOp",EDGE,"E14.2.0.1")])]})]});
            var Q21;
            Q21=makeQuery(id+"F7.boolean.opBoolean","INTERSECT",EDGE,{"derivedFrom":[makeQuery(id+"F3.opExtrude","SWEPT_FACE",FACE,{"disambiguationData":[OSD([sQuery(id+"F2.wireOp",EDGE,"E7.left")])]}),makeQuery(id+"F7.opExtrude","SWEPT_FACE",FACE,{"disambiguationData":[OSD([sQuery(id+"F6.wireOp",EDGE,"E14.1.0.1")])]})]});
            var Q22;
            Q22=makeQuery(id+"F7.boolean.opBoolean","INTERSECT",EDGE,{"derivedFrom":[makeQuery(id+"F3.opExtrude","SWEPT_FACE",FACE,{"disambiguationData":[OSD([sQuery(id+"F2.wireOp",EDGE,"E7.left")])]}),makeQuery(id+"F7.opExtrude","SWEPT_FACE",FACE,{"disambiguationData":[OSD([sQuery(id+"F6.wireOp",EDGE,"E12")])]})]});
            var Q23;
            Q23=makeQuery(id+"F1.opExtrude","SWEPT_FACE",FACE,{"disambiguationData":[OSD([sQuery(id+"F0.wireOp",EDGE,"E3.MirrorCS")])]});
            var Q24;
            {var subQ0=sQuery(id+"F2.wireOp",EDGE,"E6.right");Q24=makeQuery(id+"F7.boolean.opBoolean","SPLIT",EDGE,{"disambiguationData":[TD([makeQuery(id+"F7.opExtrude","SWEPT_FACE",FACE,{"disambiguationData":[OSD([sQuery(id+"F6.wireOp",EDGE,"E14.1.0.0")])]})])],"derivedFrom":makeQuery(id+"F3.opExtrude","CAP_EDGE",EDGE,{"disambiguationData":[OSD([subQ0])],"isStart":true})});}
            var Q25;
            {var subQ0=sQuery(id+"F2.wireOp",EDGE,"E6.right");Q25=makeQuery(id+"F7.boolean.opBoolean","SPLIT",EDGE,{"disambiguationData":[TD([makeQuery(id+"F7.opExtrude","SWEPT_FACE",FACE,{"disambiguationData":[OSD([sQuery(id+"F6.wireOp",EDGE,"E13")])]})])],"derivedFrom":makeQuery(id+"F3.opExtrude","CAP_EDGE",EDGE,{"disambiguationData":[OSD([subQ0])],"isStart":true})});}
            var Q26;
            {var subQ0=sQuery(id+"F2.wireOp",EDGE,"E6.right");var subQ1=sQuery(id+"F2.wireOp",EDGE,"E6.top");Q26=makeQuery(id+"F7.boolean.opBoolean","SPLIT",EDGE,{"disambiguationData":[TD([makeQuery(id+"F3.opExtrude","SWEPT_FACE",FACE,{"disambiguationData":[OSD([subQ1])]})])],"derivedFrom":makeQuery(id+"F3.opExtrude","CAP_EDGE",EDGE,{"disambiguationData":[OSD([subQ0])],"isStart":true})});}
            var Q27;
            {var subQ0=sQuery(id+"F2.wireOp",EDGE,"E6.right");Q27=makeQuery(id+"F7.boolean.opBoolean","SPLIT",EDGE,{"disambiguationData":[TD([makeQuery(id+"F7.opExtrude","SWEPT_FACE",FACE,{"disambiguationData":[OSD([sQuery(id+"F6.wireOp",EDGE,"E14.2.0.0")])]})])],"derivedFrom":makeQuery(id+"F3.opExtrude","CAP_EDGE",EDGE,{"disambiguationData":[OSD([subQ0])],"isStart":true})});}
            var Q28;
            {var subQ0=sQuery(id+"F2.wireOp",EDGE,"E6.right");Q28=makeQuery(id+"F7.boolean.opBoolean","SPLIT",EDGE,{"disambiguationData":[TD([makeQuery(id+"F7.opExtrude","SWEPT_FACE",FACE,{"disambiguationData":[OSD([sQuery(id+"F6.wireOp",EDGE,"E14.3.0.0")])]})])],"derivedFrom":makeQuery(id+"F3.opExtrude","CAP_EDGE",EDGE,{"disambiguationData":[OSD([subQ0])],"isStart":true})});}
            var Q29;
            {var subQ0=sQuery(id+"F2.wireOp",EDGE,"E6.bottom");var subQ1=sQuery(id+"F2.wireOp",EDGE,"E6.right");Q29=makeQuery(id+"F7.boolean.opBoolean","SPLIT",EDGE,{"disambiguationData":[TD([makeQuery(id+"F3.opExtrude","SWEPT_FACE",FACE,{"disambiguationData":[OSD([subQ0])]})])],"derivedFrom":makeQuery(id+"F3.opExtrude","CAP_EDGE",EDGE,{"disambiguationData":[OSD([subQ1])],"isStart":true})});}
            var Q30;
            Q30=makeQuery(id+"F7.boolean.opBoolean","INTERSECT",EDGE,{"derivedFrom":[makeQuery(id+"F3.opExtrude","SWEPT_FACE",FACE,{"disambiguationData":[OSD([sQuery(id+"F2.wireOp",EDGE,"E6.right")])]}),makeQuery(id+"F7.opExtrude","SWEPT_FACE",FACE,{"disambiguationData":[OSD([sQuery(id+"F6.wireOp",EDGE,"E14.4.0.1")])]})]});
            var Q31;
            Q31=makeQuery(id+"F7.boolean.opBoolean","INTERSECT",EDGE,{"derivedFrom":[makeQuery(id+"F3.opExtrude","SWEPT_FACE",FACE,{"disambiguationData":[OSD([sQuery(id+"F2.wireOp",EDGE,"E6.right")])]}),makeQuery(id+"F7.opExtrude","SWEPT_FACE",FACE,{"disambiguationData":[OSD([sQuery(id+"F6.wireOp",EDGE,"E14.3.0.1")])]})]});
            var Q32;
            Q32=makeQuery(id+"F7.boolean.opBoolean","INTERSECT",EDGE,{"derivedFrom":[makeQuery(id+"F3.opExtrude","SWEPT_FACE",FACE,{"disambiguationData":[OSD([sQuery(id+"F2.wireOp",EDGE,"E6.right")])]}),makeQuery(id+"F7.opExtrude","SWEPT_FACE",FACE,{"disambiguationData":[OSD([sQuery(id+"F6.wireOp",EDGE,"E14.2.0.1")])]})]});
            var Q33;
            Q33=makeQuery(id+"F7.boolean.opBoolean","INTERSECT",EDGE,{"derivedFrom":[makeQuery(id+"F3.opExtrude","SWEPT_FACE",FACE,{"disambiguationData":[OSD([sQuery(id+"F2.wireOp",EDGE,"E6.right")])]}),makeQuery(id+"F7.opExtrude","SWEPT_FACE",FACE,{"disambiguationData":[OSD([sQuery(id+"F6.wireOp",EDGE,"E14.1.0.1")])]})]});
            var Q34;
            Q34=makeQuery(id+"F7.boolean.opBoolean","INTERSECT",EDGE,{"derivedFrom":[makeQuery(id+"F3.opExtrude","SWEPT_FACE",FACE,{"disambiguationData":[OSD([sQuery(id+"F2.wireOp",EDGE,"E6.right")])]}),makeQuery(id+"F7.opExtrude","SWEPT_FACE",FACE,{"disambiguationData":[OSD([sQuery(id+"F6.wireOp",EDGE,"E12")])]})]});
            var Q35;
            {var subQ0=sQuery(id+"F2.wireOp",EDGE,"E7.right");var subQ1=sQuery(id+"F2.wireOp",EDGE,"E7.top");Q35=makeQuery(id+"F7.boolean.opBoolean","SPLIT",EDGE,{"disambiguationData":[TD([makeQuery(id+"F3.opExtrude","SWEPT_FACE",FACE,{"disambiguationData":[OSD([subQ1])]})])],"derivedFrom":makeQuery(id+"F3.opExtrude","CAP_EDGE",EDGE,{"disambiguationData":[OSD([subQ0])],"isStart":false})});}
            var Q36;
            Q36=makeQuery(id+"F9.boolean.opBoolean","INTERSECT",EDGE,{"derivedFrom":[makeQuery(id+"F7.boolean.opBoolean","COPY",FACE,{"disambiguationData":[TD([makeQuery(id+"F3.opExtrude","SWEPT_FACE",FACE,{"disambiguationData":[OSD([sQuery(id+"F2.wireOp",EDGE,"E7.left")])]})])],"derivedFrom":makeQuery(id+"F7.opExtrude","SWEPT_FACE",FACE,{"disambiguationData":[OSD([sQuery(id+"F6.wireOp",EDGE,"E32.MirrorCS")])]})}),makeQuery(id+"F9.opExtrude","SWEPT_FACE",FACE,{"disambiguationData":[OSD([sQuery(id+"F8.wireOp",EDGE,"E65.MirrorCS")])]})]});
            var Q37;
            {var subQ0=sQuery(id+"F2.wireOp",EDGE,"E7.right");Q37=makeQuery(id+"F7.boolean.opBoolean","SPLIT",EDGE,{"disambiguationData":[TD([makeQuery(id+"F7.opExtrude","SWEPT_FACE",FACE,{"disambiguationData":[OSD([sQuery(id+"F6.wireOp",EDGE,"E24.MirrorCS")])]})])],"derivedFrom":makeQuery(id+"F3.opExtrude","CAP_EDGE",EDGE,{"disambiguationData":[OSD([subQ0])],"isStart":false})});}
            var Q38;
            Q38=makeQuery(id+"F9.boolean.opBoolean","INTERSECT",EDGE,{"derivedFrom":[makeQuery(id+"F7.boolean.opBoolean","COPY",FACE,{"disambiguationData":[TD([makeQuery(id+"F3.opExtrude","SWEPT_FACE",FACE,{"disambiguationData":[OSD([sQuery(id+"F2.wireOp",EDGE,"E7.left")])]})])],"derivedFrom":makeQuery(id+"F7.opExtrude","SWEPT_FACE",FACE,{"disambiguationData":[OSD([sQuery(id+"F6.wireOp",EDGE,"E40.MirrorCS")])]})}),makeQuery(id+"F9.opExtrude","SWEPT_FACE",FACE,{"disambiguationData":[OSD([sQuery(id+"F8.wireOp",EDGE,"E56.MirrorCS")])]})]});
            var Q39;
            {var subQ0=sQuery(id+"F2.wireOp",EDGE,"E7.right");Q39=makeQuery(id+"F7.boolean.opBoolean","SPLIT",EDGE,{"disambiguationData":[TD([makeQuery(id+"F7.opExtrude","SWEPT_FACE",FACE,{"disambiguationData":[OSD([sQuery(id+"F6.wireOp",EDGE,"E25.MirrorCS")])]})])],"derivedFrom":makeQuery(id+"F3.opExtrude","CAP_EDGE",EDGE,{"disambiguationData":[OSD([subQ0])],"isStart":false})});}
            var Q40;
            Q40=makeQuery(id+"F9.boolean.opBoolean","INTERSECT",EDGE,{"derivedFrom":[makeQuery(id+"F7.boolean.opBoolean","COPY",FACE,{"disambiguationData":[TD([makeQuery(id+"F3.opExtrude","SWEPT_FACE",FACE,{"disambiguationData":[OSD([sQuery(id+"F2.wireOp",EDGE,"E7.left")])]})])],"derivedFrom":makeQuery(id+"F7.opExtrude","SWEPT_FACE",FACE,{"disambiguationData":[OSD([sQuery(id+"F6.wireOp",EDGE,"E41.MirrorCS")])]})}),makeQuery(id+"F9.opExtrude","SWEPT_FACE",FACE,{"disambiguationData":[OSD([sQuery(id+"F8.wireOp",EDGE,"E59.MirrorCS")])]})]});
            var Q41;
            {var subQ0=sQuery(id+"F2.wireOp",EDGE,"E7.right");Q41=makeQuery(id+"F7.boolean.opBoolean","SPLIT",EDGE,{"disambiguationData":[TD([makeQuery(id+"F7.opExtrude","SWEPT_FACE",FACE,{"disambiguationData":[OSD([sQuery(id+"F6.wireOp",EDGE,"E22.MirrorCS")])]})])],"derivedFrom":makeQuery(id+"F3.opExtrude","CAP_EDGE",EDGE,{"disambiguationData":[OSD([subQ0])],"isStart":false})});}
            var Q42;
            Q42=makeQuery(id+"F9.boolean.opBoolean","INTERSECT",EDGE,{"derivedFrom":[makeQuery(id+"F7.boolean.opBoolean","COPY",FACE,{"disambiguationData":[TD([makeQuery(id+"F3.opExtrude","SWEPT_FACE",FACE,{"disambiguationData":[OSD([sQuery(id+"F2.wireOp",EDGE,"E7.left")])]})])],"derivedFrom":makeQuery(id+"F7.opExtrude","SWEPT_FACE",FACE,{"disambiguationData":[OSD([sQuery(id+"F6.wireOp",EDGE,"E33.MirrorCS")])]})}),makeQuery(id+"F9.opExtrude","SWEPT_FACE",FACE,{"disambiguationData":[OSD([sQuery(id+"F8.wireOp",EDGE,"E58.MirrorCS")])]})]});
            var Q43;
            {var subQ0=sQuery(id+"F2.wireOp",EDGE,"E7.right");Q43=makeQuery(id+"F7.boolean.opBoolean","SPLIT",EDGE,{"disambiguationData":[TD([makeQuery(id+"F7.opExtrude","SWEPT_FACE",FACE,{"disambiguationData":[OSD([sQuery(id+"F6.wireOp",EDGE,"E29.MirrorCS")])]})])],"derivedFrom":makeQuery(id+"F3.opExtrude","CAP_EDGE",EDGE,{"disambiguationData":[OSD([subQ0])],"isStart":false})});}
            var Q44;
            Q44=makeQuery(id+"F9.boolean.opBoolean","INTERSECT",EDGE,{"derivedFrom":[makeQuery(id+"F7.boolean.opBoolean","COPY",FACE,{"disambiguationData":[TD([makeQuery(id+"F3.opExtrude","SWEPT_FACE",FACE,{"disambiguationData":[OSD([sQuery(id+"F2.wireOp",EDGE,"E7.left")])]})])],"derivedFrom":makeQuery(id+"F7.opExtrude","SWEPT_FACE",FACE,{"disambiguationData":[OSD([sQuery(id+"F6.wireOp",EDGE,"E37.MirrorCS")])]})}),makeQuery(id+"F9.opExtrude","SWEPT_FACE",FACE,{"disambiguationData":[OSD([sQuery(id+"F8.wireOp",EDGE,"E53.MirrorCS")])]})]});
            var Q45;
            {var subQ0=sQuery(id+"F2.wireOp",EDGE,"E7.bottom");var subQ1=sQuery(id+"F2.wireOp",EDGE,"E7.right");Q45=makeQuery(id+"F7.boolean.opBoolean","SPLIT",EDGE,{"disambiguationData":[TD([makeQuery(id+"F3.opExtrude","SWEPT_FACE",FACE,{"disambiguationData":[OSD([subQ0])]})])],"derivedFrom":makeQuery(id+"F3.opExtrude","CAP_EDGE",EDGE,{"disambiguationData":[OSD([subQ1])],"isStart":false})});}
            var Q46;
            {var subQ0=sQuery(id+"F2.wireOp",EDGE,"E7.left");var subQ1=sQuery(id+"F2.wireOp",EDGE,"E7.top");Q46=makeQuery(id+"F7.boolean.opBoolean","SPLIT",EDGE,{"disambiguationData":[TD([makeQuery(id+"F3.opExtrude","SWEPT_FACE",FACE,{"disambiguationData":[OSD([subQ1])]})])],"derivedFrom":makeQuery(id+"F3.opExtrude","CAP_EDGE",EDGE,{"disambiguationData":[OSD([subQ0])],"isStart":false})});}
            var Q47;
            Q47=makeQuery(id+"F7.boolean.opBoolean","INTERSECT",EDGE,{"derivedFrom":[makeQuery(id+"F3.opExtrude","SWEPT_FACE",FACE,{"disambiguationData":[OSD([sQuery(id+"F2.wireOp",EDGE,"E7.left")])]}),makeQuery(id+"F7.opExtrude","SWEPT_FACE",FACE,{"disambiguationData":[OSD([sQuery(id+"F6.wireOp",EDGE,"E32.MirrorCS")])]})]});
            var Q48;
            {var subQ0=sQuery(id+"F2.wireOp",EDGE,"E7.left");Q48=makeQuery(id+"F7.boolean.opBoolean","SPLIT",EDGE,{"disambiguationData":[TD([makeQuery(id+"F7.opExtrude","SWEPT_FACE",FACE,{"disambiguationData":[OSD([sQuery(id+"F6.wireOp",EDGE,"E24.MirrorCS")])]})])],"derivedFrom":makeQuery(id+"F3.opExtrude","CAP_EDGE",EDGE,{"disambiguationData":[OSD([subQ0])],"isStart":false})});}
            var Q49;
            Q49=makeQuery(id+"F7.boolean.opBoolean","INTERSECT",EDGE,{"derivedFrom":[makeQuery(id+"F3.opExtrude","SWEPT_FACE",FACE,{"disambiguationData":[OSD([sQuery(id+"F2.wireOp",EDGE,"E7.left")])]}),makeQuery(id+"F7.opExtrude","SWEPT_FACE",FACE,{"disambiguationData":[OSD([sQuery(id+"F6.wireOp",EDGE,"E40.MirrorCS")])]})]});
            var Q50;
            {var subQ0=sQuery(id+"F2.wireOp",EDGE,"E7.left");Q50=makeQuery(id+"F7.boolean.opBoolean","SPLIT",EDGE,{"disambiguationData":[TD([makeQuery(id+"F7.opExtrude","SWEPT_FACE",FACE,{"disambiguationData":[OSD([sQuery(id+"F6.wireOp",EDGE,"E25.MirrorCS")])]})])],"derivedFrom":makeQuery(id+"F3.opExtrude","CAP_EDGE",EDGE,{"disambiguationData":[OSD([subQ0])],"isStart":false})});}
            var Q51;
            Q51=makeQuery(id+"F7.boolean.opBoolean","INTERSECT",EDGE,{"derivedFrom":[makeQuery(id+"F3.opExtrude","SWEPT_FACE",FACE,{"disambiguationData":[OSD([sQuery(id+"F2.wireOp",EDGE,"E7.left")])]}),makeQuery(id+"F7.opExtrude","SWEPT_FACE",FACE,{"disambiguationData":[OSD([sQuery(id+"F6.wireOp",EDGE,"E41.MirrorCS")])]})]});
            var Q52;
            {var subQ0=sQuery(id+"F2.wireOp",EDGE,"E7.left");Q52=makeQuery(id+"F7.boolean.opBoolean","SPLIT",EDGE,{"disambiguationData":[TD([makeQuery(id+"F7.opExtrude","SWEPT_FACE",FACE,{"disambiguationData":[OSD([sQuery(id+"F6.wireOp",EDGE,"E22.MirrorCS")])]})])],"derivedFrom":makeQuery(id+"F3.opExtrude","CAP_EDGE",EDGE,{"disambiguationData":[OSD([subQ0])],"isStart":false})});}
            var Q53;
            Q53=makeQuery(id+"F7.boolean.opBoolean","INTERSECT",EDGE,{"derivedFrom":[makeQuery(id+"F3.opExtrude","SWEPT_FACE",FACE,{"disambiguationData":[OSD([sQuery(id+"F2.wireOp",EDGE,"E7.left")])]}),makeQuery(id+"F7.opExtrude","SWEPT_FACE",FACE,{"disambiguationData":[OSD([sQuery(id+"F6.wireOp",EDGE,"E33.MirrorCS")])]})]});
            var Q54;
            {var subQ0=sQuery(id+"F2.wireOp",EDGE,"E7.left");Q54=makeQuery(id+"F7.boolean.opBoolean","SPLIT",EDGE,{"disambiguationData":[TD([makeQuery(id+"F7.opExtrude","SWEPT_FACE",FACE,{"disambiguationData":[OSD([sQuery(id+"F6.wireOp",EDGE,"E29.MirrorCS")])]})])],"derivedFrom":makeQuery(id+"F3.opExtrude","CAP_EDGE",EDGE,{"disambiguationData":[OSD([subQ0])],"isStart":false})});}
            var Q55;
            Q55=makeQuery(id+"F7.boolean.opBoolean","INTERSECT",EDGE,{"derivedFrom":[makeQuery(id+"F3.opExtrude","SWEPT_FACE",FACE,{"disambiguationData":[OSD([sQuery(id+"F2.wireOp",EDGE,"E7.left")])]}),makeQuery(id+"F7.opExtrude","SWEPT_FACE",FACE,{"disambiguationData":[OSD([sQuery(id+"F6.wireOp",EDGE,"E37.MirrorCS")])]})]});
            var Q56;
            {var subQ0=sQuery(id+"F2.wireOp",EDGE,"E7.bottom");var subQ1=sQuery(id+"F2.wireOp",EDGE,"E7.left");Q56=makeQuery(id+"F7.boolean.opBoolean","SPLIT",EDGE,{"disambiguationData":[TD([makeQuery(id+"F3.opExtrude","SWEPT_FACE",FACE,{"disambiguationData":[OSD([subQ0])]})])],"derivedFrom":makeQuery(id+"F3.opExtrude","CAP_EDGE",EDGE,{"disambiguationData":[OSD([subQ1])],"isStart":false})});}
            var Q57;
            {var subQ0=sQuery(id+"F2.wireOp",EDGE,"E6.bottom");var subQ1=sQuery(id+"F2.wireOp",EDGE,"E6.right");Q57=makeQuery(id+"F7.boolean.opBoolean","SPLIT",EDGE,{"disambiguationData":[TD([makeQuery(id+"F3.opExtrude","SWEPT_FACE",FACE,{"disambiguationData":[OSD([subQ0])]})])],"derivedFrom":makeQuery(id+"F3.opExtrude","CAP_EDGE",EDGE,{"disambiguationData":[OSD([subQ1])],"isStart":false})});}
            var Q58;
            Q58=makeQuery(id+"F7.boolean.opBoolean","INTERSECT",EDGE,{"derivedFrom":[makeQuery(id+"F3.opExtrude","SWEPT_FACE",FACE,{"disambiguationData":[OSD([sQuery(id+"F2.wireOp",EDGE,"E6.right")])]}),makeQuery(id+"F7.opExtrude","SWEPT_FACE",FACE,{"disambiguationData":[OSD([sQuery(id+"F6.wireOp",EDGE,"E37.MirrorCS")])]})]});
            var Q59;
            {var subQ0=sQuery(id+"F2.wireOp",EDGE,"E6.right");Q59=makeQuery(id+"F7.boolean.opBoolean","SPLIT",EDGE,{"disambiguationData":[TD([makeQuery(id+"F7.opExtrude","SWEPT_FACE",FACE,{"disambiguationData":[OSD([sQuery(id+"F6.wireOp",EDGE,"E29.MirrorCS")])]})])],"derivedFrom":makeQuery(id+"F3.opExtrude","CAP_EDGE",EDGE,{"disambiguationData":[OSD([subQ0])],"isStart":false})});}
            var Q60;
            Q60=makeQuery(id+"F7.boolean.opBoolean","INTERSECT",EDGE,{"derivedFrom":[makeQuery(id+"F3.opExtrude","SWEPT_FACE",FACE,{"disambiguationData":[OSD([sQuery(id+"F2.wireOp",EDGE,"E6.right")])]}),makeQuery(id+"F7.opExtrude","SWEPT_FACE",FACE,{"disambiguationData":[OSD([sQuery(id+"F6.wireOp",EDGE,"E33.MirrorCS")])]})]});
            var Q61;
            {var subQ0=sQuery(id+"F2.wireOp",EDGE,"E6.right");Q61=makeQuery(id+"F7.boolean.opBoolean","SPLIT",EDGE,{"disambiguationData":[TD([makeQuery(id+"F7.opExtrude","SWEPT_FACE",FACE,{"disambiguationData":[OSD([sQuery(id+"F6.wireOp",EDGE,"E22.MirrorCS")])]})])],"derivedFrom":makeQuery(id+"F3.opExtrude","CAP_EDGE",EDGE,{"disambiguationData":[OSD([subQ0])],"isStart":false})});}
            var Q62;
            Q62=makeQuery(id+"F7.boolean.opBoolean","INTERSECT",EDGE,{"derivedFrom":[makeQuery(id+"F3.opExtrude","SWEPT_FACE",FACE,{"disambiguationData":[OSD([sQuery(id+"F2.wireOp",EDGE,"E6.right")])]}),makeQuery(id+"F7.opExtrude","SWEPT_FACE",FACE,{"disambiguationData":[OSD([sQuery(id+"F6.wireOp",EDGE,"E41.MirrorCS")])]})]});
            var Q63;
            {var subQ0=sQuery(id+"F2.wireOp",EDGE,"E6.right");Q63=makeQuery(id+"F7.boolean.opBoolean","SPLIT",EDGE,{"disambiguationData":[TD([makeQuery(id+"F7.opExtrude","SWEPT_FACE",FACE,{"disambiguationData":[OSD([sQuery(id+"F6.wireOp",EDGE,"E25.MirrorCS")])]})])],"derivedFrom":makeQuery(id+"F3.opExtrude","CAP_EDGE",EDGE,{"disambiguationData":[OSD([subQ0])],"isStart":false})});}
            var Q64;
            Q64=makeQuery(id+"F7.boolean.opBoolean","INTERSECT",EDGE,{"derivedFrom":[makeQuery(id+"F3.opExtrude","SWEPT_FACE",FACE,{"disambiguationData":[OSD([sQuery(id+"F2.wireOp",EDGE,"E6.right")])]}),makeQuery(id+"F7.opExtrude","SWEPT_FACE",FACE,{"disambiguationData":[OSD([sQuery(id+"F6.wireOp",EDGE,"E40.MirrorCS")])]})]});
            var Q65;
            {var subQ0=sQuery(id+"F2.wireOp",EDGE,"E6.right");Q65=makeQuery(id+"F7.boolean.opBoolean","SPLIT",EDGE,{"disambiguationData":[TD([makeQuery(id+"F7.opExtrude","SWEPT_FACE",FACE,{"disambiguationData":[OSD([sQuery(id+"F6.wireOp",EDGE,"E24.MirrorCS")])]})])],"derivedFrom":makeQuery(id+"F3.opExtrude","CAP_EDGE",EDGE,{"disambiguationData":[OSD([subQ0])],"isStart":false})});}
            var Q66;
            Q66=makeQuery(id+"F7.boolean.opBoolean","INTERSECT",EDGE,{"derivedFrom":[makeQuery(id+"F3.opExtrude","SWEPT_FACE",FACE,{"disambiguationData":[OSD([sQuery(id+"F2.wireOp",EDGE,"E6.right")])]}),makeQuery(id+"F7.opExtrude","SWEPT_FACE",FACE,{"disambiguationData":[OSD([sQuery(id+"F6.wireOp",EDGE,"E32.MirrorCS")])]})]});
            var Q67;
            {var subQ0=sQuery(id+"F2.wireOp",EDGE,"E6.right");var subQ1=sQuery(id+"F2.wireOp",EDGE,"E6.top");Q67=makeQuery(id+"F7.boolean.opBoolean","SPLIT",EDGE,{"disambiguationData":[TD([makeQuery(id+"F3.opExtrude","SWEPT_FACE",FACE,{"disambiguationData":[OSD([subQ1])]})])],"derivedFrom":makeQuery(id+"F3.opExtrude","CAP_EDGE",EDGE,{"disambiguationData":[OSD([subQ0])],"isStart":false})});}
            var Q68;
            {var subQ0=sQuery(id+"F2.wireOp",EDGE,"E6.left");var subQ1=sQuery(id+"F2.wireOp",EDGE,"E6.top");Q68=makeQuery(id+"F7.boolean.opBoolean","SPLIT",EDGE,{"disambiguationData":[TD([makeQuery(id+"F3.opExtrude","SWEPT_FACE",FACE,{"disambiguationData":[OSD([subQ1])]})])],"derivedFrom":makeQuery(id+"F3.opExtrude","CAP_EDGE",EDGE,{"disambiguationData":[OSD([subQ0])],"isStart":false})});}
            var Q69;
            {var subQ0=sQuery(id+"F2.wireOp",EDGE,"E6.left");Q69=makeQuery(id+"F7.boolean.opBoolean","SPLIT",EDGE,{"disambiguationData":[TD([makeQuery(id+"F7.opExtrude","SWEPT_FACE",FACE,{"disambiguationData":[OSD([sQuery(id+"F6.wireOp",EDGE,"E24.MirrorCS")])]})])],"derivedFrom":makeQuery(id+"F3.opExtrude","CAP_EDGE",EDGE,{"disambiguationData":[OSD([subQ0])],"isStart":false})});}
            var Q70;
            Q70=makeQuery(id+"F7.boolean.opBoolean","INTERSECT",EDGE,{"derivedFrom":[makeQuery(id+"F3.opExtrude","SWEPT_FACE",FACE,{"disambiguationData":[OSD([sQuery(id+"F2.wireOp",EDGE,"E6.left")])]}),makeQuery(id+"F7.opExtrude","SWEPT_FACE",FACE,{"disambiguationData":[OSD([sQuery(id+"F6.wireOp",EDGE,"E40.MirrorCS")])]})]});
            var Q71;
            {var subQ0=sQuery(id+"F2.wireOp",EDGE,"E6.left");Q71=makeQuery(id+"F7.boolean.opBoolean","SPLIT",EDGE,{"disambiguationData":[TD([makeQuery(id+"F7.opExtrude","SWEPT_FACE",FACE,{"disambiguationData":[OSD([sQuery(id+"F6.wireOp",EDGE,"E25.MirrorCS")])]})])],"derivedFrom":makeQuery(id+"F3.opExtrude","CAP_EDGE",EDGE,{"disambiguationData":[OSD([subQ0])],"isStart":false})});}
            var Q72;
            Q72=makeQuery(id+"F7.boolean.opBoolean","INTERSECT",EDGE,{"derivedFrom":[makeQuery(id+"F3.opExtrude","SWEPT_FACE",FACE,{"disambiguationData":[OSD([sQuery(id+"F2.wireOp",EDGE,"E6.left")])]}),makeQuery(id+"F7.opExtrude","SWEPT_FACE",FACE,{"disambiguationData":[OSD([sQuery(id+"F6.wireOp",EDGE,"E41.MirrorCS")])]})]});
            var Q73;
            {var subQ0=sQuery(id+"F2.wireOp",EDGE,"E6.left");Q73=makeQuery(id+"F7.boolean.opBoolean","SPLIT",EDGE,{"disambiguationData":[TD([makeQuery(id+"F7.opExtrude","SWEPT_FACE",FACE,{"disambiguationData":[OSD([sQuery(id+"F6.wireOp",EDGE,"E22.MirrorCS")])]})])],"derivedFrom":makeQuery(id+"F3.opExtrude","CAP_EDGE",EDGE,{"disambiguationData":[OSD([subQ0])],"isStart":false})});}
            var Q74;
            Q74=makeQuery(id+"F7.boolean.opBoolean","INTERSECT",EDGE,{"derivedFrom":[makeQuery(id+"F3.opExtrude","SWEPT_FACE",FACE,{"disambiguationData":[OSD([sQuery(id+"F2.wireOp",EDGE,"E6.left")])]}),makeQuery(id+"F7.opExtrude","SWEPT_FACE",FACE,{"disambiguationData":[OSD([sQuery(id+"F6.wireOp",EDGE,"E33.MirrorCS")])]})]});
            var Q75;
            {var subQ0=sQuery(id+"F2.wireOp",EDGE,"E6.left");Q75=makeQuery(id+"F7.boolean.opBoolean","SPLIT",EDGE,{"disambiguationData":[TD([makeQuery(id+"F7.opExtrude","SWEPT_FACE",FACE,{"disambiguationData":[OSD([sQuery(id+"F6.wireOp",EDGE,"E29.MirrorCS")])]})])],"derivedFrom":makeQuery(id+"F3.opExtrude","CAP_EDGE",EDGE,{"disambiguationData":[OSD([subQ0])],"isStart":false})});}
            var Q76;
            Q76=makeQuery(id+"F7.boolean.opBoolean","INTERSECT",EDGE,{"derivedFrom":[makeQuery(id+"F3.opExtrude","SWEPT_FACE",FACE,{"disambiguationData":[OSD([sQuery(id+"F2.wireOp",EDGE,"E6.left")])]}),makeQuery(id+"F7.opExtrude","SWEPT_FACE",FACE,{"disambiguationData":[OSD([sQuery(id+"F6.wireOp",EDGE,"E37.MirrorCS")])]})]});
            var Q77;
            {var subQ0=sQuery(id+"F2.wireOp",EDGE,"E6.bottom");var subQ1=sQuery(id+"F2.wireOp",EDGE,"E6.left");Q77=makeQuery(id+"F7.boolean.opBoolean","SPLIT",EDGE,{"disambiguationData":[TD([makeQuery(id+"F3.opExtrude","SWEPT_FACE",FACE,{"disambiguationData":[OSD([subQ0])]})])],"derivedFrom":makeQuery(id+"F3.opExtrude","CAP_EDGE",EDGE,{"disambiguationData":[OSD([subQ1])],"isStart":false})});}
            var Q78;
            Q78=makeQuery(id+"F7.boolean.opBoolean","INTERSECT",EDGE,{"derivedFrom":[makeQuery(id+"F3.opExtrude","SWEPT_FACE",FACE,{"disambiguationData":[OSD([sQuery(id+"F2.wireOp",EDGE,"E6.left")])]}),makeQuery(id+"F7.opExtrude","SWEPT_FACE",FACE,{"disambiguationData":[OSD([sQuery(id+"F6.wireOp",EDGE,"E32.MirrorCS")])]})]});
            var Q79;
            {var subQ0=sQuery(id+"F2.wireOp",EDGE,"E5.left");var subQ1=sQuery(id+"F2.wireOp",EDGE,"E5.top");Q79=makeQuery(id+"F7.boolean.opBoolean","SPLIT",EDGE,{"disambiguationData":[TD([makeQuery(id+"F3.opExtrude","SWEPT_FACE",FACE,{"disambiguationData":[OSD([subQ1])]})])],"derivedFrom":makeQuery(id+"F3.opExtrude","CAP_EDGE",EDGE,{"disambiguationData":[OSD([subQ0])],"isStart":false})});}
            var Q80;
            Q80=makeQuery(id+"F7.boolean.opBoolean","INTERSECT",EDGE,{"derivedFrom":[makeQuery(id+"F3.opExtrude","SWEPT_FACE",FACE,{"disambiguationData":[OSD([sQuery(id+"F2.wireOp",EDGE,"E5.left")])]}),makeQuery(id+"F7.opExtrude","SWEPT_FACE",FACE,{"disambiguationData":[OSD([sQuery(id+"F6.wireOp",EDGE,"E32.MirrorCS")])]})]});
            var Q81;
            {var subQ0=sQuery(id+"F2.wireOp",EDGE,"E5.left");Q81=makeQuery(id+"F7.boolean.opBoolean","SPLIT",EDGE,{"disambiguationData":[TD([makeQuery(id+"F7.opExtrude","SWEPT_FACE",FACE,{"disambiguationData":[OSD([sQuery(id+"F6.wireOp",EDGE,"E24.MirrorCS")])]})])],"derivedFrom":makeQuery(id+"F3.opExtrude","CAP_EDGE",EDGE,{"disambiguationData":[OSD([subQ0])],"isStart":false})});}
            var Q82;
            Q82=makeQuery(id+"F7.boolean.opBoolean","INTERSECT",EDGE,{"derivedFrom":[makeQuery(id+"F3.opExtrude","SWEPT_FACE",FACE,{"disambiguationData":[OSD([sQuery(id+"F2.wireOp",EDGE,"E5.left")])]}),makeQuery(id+"F7.opExtrude","SWEPT_FACE",FACE,{"disambiguationData":[OSD([sQuery(id+"F6.wireOp",EDGE,"E40.MirrorCS")])]})]});
            var Q83;
            {var subQ0=sQuery(id+"F2.wireOp",EDGE,"E5.left");Q83=makeQuery(id+"F7.boolean.opBoolean","SPLIT",EDGE,{"disambiguationData":[TD([makeQuery(id+"F7.opExtrude","SWEPT_FACE",FACE,{"disambiguationData":[OSD([sQuery(id+"F6.wireOp",EDGE,"E25.MirrorCS")])]})])],"derivedFrom":makeQuery(id+"F3.opExtrude","CAP_EDGE",EDGE,{"disambiguationData":[OSD([subQ0])],"isStart":false})});}
            var Q84;
            Q84=makeQuery(id+"F7.boolean.opBoolean","INTERSECT",EDGE,{"derivedFrom":[makeQuery(id+"F3.opExtrude","SWEPT_FACE",FACE,{"disambiguationData":[OSD([sQuery(id+"F2.wireOp",EDGE,"E5.left")])]}),makeQuery(id+"F7.opExtrude","SWEPT_FACE",FACE,{"disambiguationData":[OSD([sQuery(id+"F6.wireOp",EDGE,"E41.MirrorCS")])]})]});
            var Q85;
            {var subQ0=sQuery(id+"F2.wireOp",EDGE,"E5.left");Q85=makeQuery(id+"F7.boolean.opBoolean","SPLIT",EDGE,{"disambiguationData":[TD([makeQuery(id+"F7.opExtrude","SWEPT_FACE",FACE,{"disambiguationData":[OSD([sQuery(id+"F6.wireOp",EDGE,"E22.MirrorCS")])]})])],"derivedFrom":makeQuery(id+"F3.opExtrude","CAP_EDGE",EDGE,{"disambiguationData":[OSD([subQ0])],"isStart":false})});}
            var Q86;
            Q86=makeQuery(id+"F7.boolean.opBoolean","INTERSECT",EDGE,{"derivedFrom":[makeQuery(id+"F3.opExtrude","SWEPT_FACE",FACE,{"disambiguationData":[OSD([sQuery(id+"F2.wireOp",EDGE,"E5.left")])]}),makeQuery(id+"F7.opExtrude","SWEPT_FACE",FACE,{"disambiguationData":[OSD([sQuery(id+"F6.wireOp",EDGE,"E33.MirrorCS")])]})]});
            var Q87;
            {var subQ0=sQuery(id+"F2.wireOp",EDGE,"E5.left");Q87=makeQuery(id+"F7.boolean.opBoolean","SPLIT",EDGE,{"disambiguationData":[TD([makeQuery(id+"F7.opExtrude","SWEPT_FACE",FACE,{"disambiguationData":[OSD([sQuery(id+"F6.wireOp",EDGE,"E29.MirrorCS")])]})])],"derivedFrom":makeQuery(id+"F3.opExtrude","CAP_EDGE",EDGE,{"disambiguationData":[OSD([subQ0])],"isStart":false})});}
            var Q88;
            Q88=makeQuery(id+"F7.boolean.opBoolean","INTERSECT",EDGE,{"derivedFrom":[makeQuery(id+"F3.opExtrude","SWEPT_FACE",FACE,{"disambiguationData":[OSD([sQuery(id+"F2.wireOp",EDGE,"E5.left")])]}),makeQuery(id+"F7.opExtrude","SWEPT_FACE",FACE,{"disambiguationData":[OSD([sQuery(id+"F6.wireOp",EDGE,"E37.MirrorCS")])]})]});
            var Q89;
            {var subQ0=sQuery(id+"F2.wireOp",EDGE,"E5.bottom");var subQ1=sQuery(id+"F2.wireOp",EDGE,"E5.left");Q89=makeQuery(id+"F7.boolean.opBoolean","SPLIT",EDGE,{"disambiguationData":[TD([makeQuery(id+"F3.opExtrude","SWEPT_FACE",FACE,{"disambiguationData":[OSD([subQ0])]})])],"derivedFrom":makeQuery(id+"F3.opExtrude","CAP_EDGE",EDGE,{"disambiguationData":[OSD([subQ1])],"isStart":false})});}
            var Q90;
            {var subQ0=sQuery(id+"F2.wireOp",EDGE,"E5.bottom");var subQ1=sQuery(id+"F2.wireOp",EDGE,"E5.right");Q90=makeQuery(id+"F7.boolean.opBoolean","SPLIT",EDGE,{"disambiguationData":[TD([makeQuery(id+"F3.opExtrude","SWEPT_FACE",FACE,{"disambiguationData":[OSD([subQ0])]})])],"derivedFrom":makeQuery(id+"F3.opExtrude","CAP_EDGE",EDGE,{"disambiguationData":[OSD([subQ1])],"isStart":false})});}
            var Q91;
            Q91=makeQuery(id+"F9.boolean.opBoolean","INTERSECT",EDGE,{"derivedFrom":[makeQuery(id+"F7.boolean.opBoolean","COPY",FACE,{"disambiguationData":[TD([makeQuery(id+"F3.opExtrude","SWEPT_FACE",FACE,{"disambiguationData":[OSD([sQuery(id+"F2.wireOp",EDGE,"E5.left")])]})])],"derivedFrom":makeQuery(id+"F7.opExtrude","SWEPT_FACE",FACE,{"disambiguationData":[OSD([sQuery(id+"F6.wireOp",EDGE,"E37.MirrorCS")])]})}),makeQuery(id+"F9.opExtrude","SWEPT_FACE",FACE,{"disambiguationData":[OSD([sQuery(id+"F8.wireOp",EDGE,"E42.left")])]})]});
            var Q92;
            {var subQ0=sQuery(id+"F2.wireOp",EDGE,"E5.right");Q92=makeQuery(id+"F7.boolean.opBoolean","SPLIT",EDGE,{"disambiguationData":[TD([makeQuery(id+"F7.opExtrude","SWEPT_FACE",FACE,{"disambiguationData":[OSD([sQuery(id+"F6.wireOp",EDGE,"E29.MirrorCS")])]})])],"derivedFrom":makeQuery(id+"F3.opExtrude","CAP_EDGE",EDGE,{"disambiguationData":[OSD([subQ0])],"isStart":false})});}
            var Q93;
            Q93=makeQuery(id+"F9.boolean.opBoolean","INTERSECT",EDGE,{"derivedFrom":[makeQuery(id+"F7.boolean.opBoolean","COPY",FACE,{"disambiguationData":[TD([makeQuery(id+"F3.opExtrude","SWEPT_FACE",FACE,{"disambiguationData":[OSD([sQuery(id+"F2.wireOp",EDGE,"E5.left")])]})])],"derivedFrom":makeQuery(id+"F7.opExtrude","SWEPT_FACE",FACE,{"disambiguationData":[OSD([sQuery(id+"F6.wireOp",EDGE,"E33.MirrorCS")])]})}),makeQuery(id+"F9.opExtrude","SWEPT_FACE",FACE,{"disambiguationData":[OSD([sQuery(id+"F8.wireOp",EDGE,"E43.0.1.3")])]})]});
            var Q94;
            {var subQ0=sQuery(id+"F2.wireOp",EDGE,"E5.right");Q94=makeQuery(id+"F7.boolean.opBoolean","SPLIT",EDGE,{"disambiguationData":[TD([makeQuery(id+"F7.opExtrude","SWEPT_FACE",FACE,{"disambiguationData":[OSD([sQuery(id+"F6.wireOp",EDGE,"E22.MirrorCS")])]})])],"derivedFrom":makeQuery(id+"F3.opExtrude","CAP_EDGE",EDGE,{"disambiguationData":[OSD([subQ0])],"isStart":false})});}
            var Q95;
            Q95=makeQuery(id+"F9.boolean.opBoolean","INTERSECT",EDGE,{"derivedFrom":[makeQuery(id+"F7.boolean.opBoolean","COPY",FACE,{"disambiguationData":[TD([makeQuery(id+"F3.opExtrude","SWEPT_FACE",FACE,{"disambiguationData":[OSD([sQuery(id+"F2.wireOp",EDGE,"E5.left")])]})])],"derivedFrom":makeQuery(id+"F7.opExtrude","SWEPT_FACE",FACE,{"disambiguationData":[OSD([sQuery(id+"F6.wireOp",EDGE,"E41.MirrorCS")])]})}),makeQuery(id+"F9.opExtrude","SWEPT_FACE",FACE,{"disambiguationData":[OSD([sQuery(id+"F8.wireOp",EDGE,"E43.0.2.3")])]})]});
            var Q96;
            {var subQ0=sQuery(id+"F2.wireOp",EDGE,"E5.right");Q96=makeQuery(id+"F7.boolean.opBoolean","SPLIT",EDGE,{"disambiguationData":[TD([makeQuery(id+"F7.opExtrude","SWEPT_FACE",FACE,{"disambiguationData":[OSD([sQuery(id+"F6.wireOp",EDGE,"E25.MirrorCS")])]})])],"derivedFrom":makeQuery(id+"F3.opExtrude","CAP_EDGE",EDGE,{"disambiguationData":[OSD([subQ0])],"isStart":false})});}
            var Q97;
            Q97=makeQuery(id+"F9.boolean.opBoolean","INTERSECT",EDGE,{"derivedFrom":[makeQuery(id+"F7.boolean.opBoolean","COPY",FACE,{"disambiguationData":[TD([makeQuery(id+"F3.opExtrude","SWEPT_FACE",FACE,{"disambiguationData":[OSD([sQuery(id+"F2.wireOp",EDGE,"E5.left")])]})])],"derivedFrom":makeQuery(id+"F7.opExtrude","SWEPT_FACE",FACE,{"disambiguationData":[OSD([sQuery(id+"F6.wireOp",EDGE,"E40.MirrorCS")])]})}),makeQuery(id+"F9.opExtrude","SWEPT_FACE",FACE,{"disambiguationData":[OSD([sQuery(id+"F8.wireOp",EDGE,"E43.0.3.3")])]})]});
            var Q98;
            {var subQ0=sQuery(id+"F2.wireOp",EDGE,"E5.right");Q98=makeQuery(id+"F7.boolean.opBoolean","SPLIT",EDGE,{"disambiguationData":[TD([makeQuery(id+"F7.opExtrude","SWEPT_FACE",FACE,{"disambiguationData":[OSD([sQuery(id+"F6.wireOp",EDGE,"E24.MirrorCS")])]})])],"derivedFrom":makeQuery(id+"F3.opExtrude","CAP_EDGE",EDGE,{"disambiguationData":[OSD([subQ0])],"isStart":false})});}
            var Q99;
            Q99=makeQuery(id+"F9.boolean.opBoolean","INTERSECT",EDGE,{"derivedFrom":[makeQuery(id+"F7.boolean.opBoolean","COPY",FACE,{"disambiguationData":[TD([makeQuery(id+"F3.opExtrude","SWEPT_FACE",FACE,{"disambiguationData":[OSD([sQuery(id+"F2.wireOp",EDGE,"E5.left")])]})])],"derivedFrom":makeQuery(id+"F7.opExtrude","SWEPT_FACE",FACE,{"disambiguationData":[OSD([sQuery(id+"F6.wireOp",EDGE,"E32.MirrorCS")])]})}),makeQuery(id+"F9.opExtrude","SWEPT_FACE",FACE,{"disambiguationData":[OSD([sQuery(id+"F8.wireOp",EDGE,"E43.0.4.3")])]})]});
            var Q100;
            {var subQ0=sQuery(id+"F2.wireOp",EDGE,"E5.right");var subQ1=sQuery(id+"F2.wireOp",EDGE,"E5.top");Q100=makeQuery(id+"F7.boolean.opBoolean","SPLIT",EDGE,{"disambiguationData":[TD([makeQuery(id+"F3.opExtrude","SWEPT_FACE",FACE,{"disambiguationData":[OSD([subQ1])]})])],"derivedFrom":makeQuery(id+"F3.opExtrude","CAP_EDGE",EDGE,{"disambiguationData":[OSD([subQ0])],"isStart":false})});}
            var Q101;
            {var subQ0=sQuery(id+"F2.wireOp",EDGE,"E5.bottom");var subQ1=sQuery(id+"F2.wireOp",EDGE,"E5.right");Q101=makeQuery(id+"F7.boolean.opBoolean","SPLIT",EDGE,{"disambiguationData":[TD([makeQuery(id+"F3.opExtrude","SWEPT_FACE",FACE,{"disambiguationData":[OSD([subQ0])]})])],"derivedFrom":makeQuery(id+"F3.opExtrude","CAP_EDGE",EDGE,{"disambiguationData":[OSD([subQ1])],"isStart":true})});}
            var Q102;
            Q102=makeQuery(id+"F9.boolean.opBoolean","INTERSECT",EDGE,{"derivedFrom":[makeQuery(id+"F7.boolean.opBoolean","COPY",FACE,{"disambiguationData":[TD([makeQuery(id+"F3.opExtrude","SWEPT_FACE",FACE,{"disambiguationData":[OSD([sQuery(id+"F2.wireOp",EDGE,"E5.left")])]})])],"derivedFrom":makeQuery(id+"F7.opExtrude","SWEPT_FACE",FACE,{"disambiguationData":[OSD([sQuery(id+"F6.wireOp",EDGE,"E14.4.0.1")])]})}),makeQuery(id+"F9.opExtrude","SWEPT_FACE",FACE,{"disambiguationData":[OSD([sQuery(id+"F8.wireOp",EDGE,"E42.left")])]})]});
            var Q103;
            {var subQ0=sQuery(id+"F2.wireOp",EDGE,"E5.right");Q103=makeQuery(id+"F7.boolean.opBoolean","SPLIT",EDGE,{"disambiguationData":[TD([makeQuery(id+"F7.opExtrude","SWEPT_FACE",FACE,{"disambiguationData":[OSD([sQuery(id+"F6.wireOp",EDGE,"E14.3.0.0")])]})])],"derivedFrom":makeQuery(id+"F3.opExtrude","CAP_EDGE",EDGE,{"disambiguationData":[OSD([subQ0])],"isStart":true})});}
            var Q104;
            Q104=makeQuery(id+"F9.boolean.opBoolean","INTERSECT",EDGE,{"derivedFrom":[makeQuery(id+"F7.boolean.opBoolean","COPY",FACE,{"disambiguationData":[TD([makeQuery(id+"F3.opExtrude","SWEPT_FACE",FACE,{"disambiguationData":[OSD([sQuery(id+"F2.wireOp",EDGE,"E5.left")])]})])],"derivedFrom":makeQuery(id+"F7.opExtrude","SWEPT_FACE",FACE,{"disambiguationData":[OSD([sQuery(id+"F6.wireOp",EDGE,"E14.3.0.1")])]})}),makeQuery(id+"F9.opExtrude","SWEPT_FACE",FACE,{"disambiguationData":[OSD([sQuery(id+"F8.wireOp",EDGE,"E43.0.1.3")])]})]});
            var Q105;
            {var subQ0=sQuery(id+"F2.wireOp",EDGE,"E5.right");Q105=makeQuery(id+"F7.boolean.opBoolean","SPLIT",EDGE,{"disambiguationData":[TD([makeQuery(id+"F7.opExtrude","SWEPT_FACE",FACE,{"disambiguationData":[OSD([sQuery(id+"F6.wireOp",EDGE,"E14.2.0.0")])]})])],"derivedFrom":makeQuery(id+"F3.opExtrude","CAP_EDGE",EDGE,{"disambiguationData":[OSD([subQ0])],"isStart":true})});}
            var Q106;
            Q106=makeQuery(id+"F9.boolean.opBoolean","INTERSECT",EDGE,{"derivedFrom":[makeQuery(id+"F7.boolean.opBoolean","COPY",FACE,{"disambiguationData":[TD([makeQuery(id+"F3.opExtrude","SWEPT_FACE",FACE,{"disambiguationData":[OSD([sQuery(id+"F2.wireOp",EDGE,"E5.left")])]})])],"derivedFrom":makeQuery(id+"F7.opExtrude","SWEPT_FACE",FACE,{"disambiguationData":[OSD([sQuery(id+"F6.wireOp",EDGE,"E14.2.0.1")])]})}),makeQuery(id+"F9.opExtrude","SWEPT_FACE",FACE,{"disambiguationData":[OSD([sQuery(id+"F8.wireOp",EDGE,"E43.0.2.3")])]})]});
            var Q107;
            {var subQ0=sQuery(id+"F2.wireOp",EDGE,"E5.right");Q107=makeQuery(id+"F7.boolean.opBoolean","SPLIT",EDGE,{"disambiguationData":[TD([makeQuery(id+"F7.opExtrude","SWEPT_FACE",FACE,{"disambiguationData":[OSD([sQuery(id+"F6.wireOp",EDGE,"E14.1.0.0")])]})])],"derivedFrom":makeQuery(id+"F3.opExtrude","CAP_EDGE",EDGE,{"disambiguationData":[OSD([subQ0])],"isStart":true})});}
            var Q108;
            Q108=makeQuery(id+"F9.boolean.opBoolean","INTERSECT",EDGE,{"derivedFrom":[makeQuery(id+"F7.boolean.opBoolean","COPY",FACE,{"disambiguationData":[TD([makeQuery(id+"F3.opExtrude","SWEPT_FACE",FACE,{"disambiguationData":[OSD([sQuery(id+"F2.wireOp",EDGE,"E5.left")])]})])],"derivedFrom":makeQuery(id+"F7.opExtrude","SWEPT_FACE",FACE,{"disambiguationData":[OSD([sQuery(id+"F6.wireOp",EDGE,"E14.1.0.1")])]})}),makeQuery(id+"F9.opExtrude","SWEPT_FACE",FACE,{"disambiguationData":[OSD([sQuery(id+"F8.wireOp",EDGE,"E43.0.3.3")])]})]});
            var Q109;
            {var subQ0=sQuery(id+"F2.wireOp",EDGE,"E5.right");Q109=makeQuery(id+"F7.boolean.opBoolean","SPLIT",EDGE,{"disambiguationData":[TD([makeQuery(id+"F7.opExtrude","SWEPT_FACE",FACE,{"disambiguationData":[OSD([sQuery(id+"F6.wireOp",EDGE,"E13")])]})])],"derivedFrom":makeQuery(id+"F3.opExtrude","CAP_EDGE",EDGE,{"disambiguationData":[OSD([subQ0])],"isStart":true})});}
            var Q110;
            Q110=makeQuery(id+"F9.boolean.opBoolean","INTERSECT",EDGE,{"derivedFrom":[makeQuery(id+"F7.boolean.opBoolean","COPY",FACE,{"disambiguationData":[TD([makeQuery(id+"F3.opExtrude","SWEPT_FACE",FACE,{"disambiguationData":[OSD([sQuery(id+"F2.wireOp",EDGE,"E5.left")])]})])],"derivedFrom":makeQuery(id+"F7.opExtrude","SWEPT_FACE",FACE,{"disambiguationData":[OSD([sQuery(id+"F6.wireOp",EDGE,"E12")])]})}),makeQuery(id+"F9.opExtrude","SWEPT_FACE",FACE,{"disambiguationData":[OSD([sQuery(id+"F8.wireOp",EDGE,"E43.0.4.3")])]})]});
            var Q111;
            {var subQ0=sQuery(id+"F2.wireOp",EDGE,"E5.right");var subQ1=sQuery(id+"F2.wireOp",EDGE,"E5.top");Q111=makeQuery(id+"F7.boolean.opBoolean","SPLIT",EDGE,{"disambiguationData":[TD([makeQuery(id+"F3.opExtrude","SWEPT_FACE",FACE,{"disambiguationData":[OSD([subQ1])]})])],"derivedFrom":makeQuery(id+"F3.opExtrude","CAP_EDGE",EDGE,{"disambiguationData":[OSD([subQ0])],"isStart":true})});}
            var Q112;
            {var subQ0=sQuery(id+"F2.wireOp",EDGE,"E6.bottom");var subQ1=sQuery(id+"F2.wireOp",EDGE,"E6.left");Q112=makeQuery(id+"F7.boolean.opBoolean","SPLIT",EDGE,{"disambiguationData":[TD([makeQuery(id+"F3.opExtrude","SWEPT_FACE",FACE,{"disambiguationData":[OSD([subQ0])]})])],"derivedFrom":makeQuery(id+"F3.opExtrude","CAP_EDGE",EDGE,{"disambiguationData":[OSD([subQ1])],"isStart":true})});}
            var Q113;
            {var subQ0=sQuery(id+"F2.wireOp",EDGE,"E6.left");Q113=makeQuery(id+"F7.boolean.opBoolean","SPLIT",EDGE,{"disambiguationData":[TD([makeQuery(id+"F7.opExtrude","SWEPT_FACE",FACE,{"disambiguationData":[OSD([sQuery(id+"F6.wireOp",EDGE,"E14.3.0.0")])]})])],"derivedFrom":makeQuery(id+"F3.opExtrude","CAP_EDGE",EDGE,{"disambiguationData":[OSD([subQ0])],"isStart":true})});}
            var Q114;
            {var subQ0=sQuery(id+"F2.wireOp",EDGE,"E6.left");Q114=makeQuery(id+"F7.boolean.opBoolean","SPLIT",EDGE,{"disambiguationData":[TD([makeQuery(id+"F7.opExtrude","SWEPT_FACE",FACE,{"disambiguationData":[OSD([sQuery(id+"F6.wireOp",EDGE,"E14.2.0.0")])]})])],"derivedFrom":makeQuery(id+"F3.opExtrude","CAP_EDGE",EDGE,{"disambiguationData":[OSD([subQ0])],"isStart":true})});}
            var Q115;
            Q115=makeQuery(id+"F7.boolean.opBoolean","INTERSECT",EDGE,{"derivedFrom":[makeQuery(id+"F3.opExtrude","SWEPT_FACE",FACE,{"disambiguationData":[OSD([sQuery(id+"F2.wireOp",EDGE,"E6.left")])]}),makeQuery(id+"F7.opExtrude","SWEPT_FACE",FACE,{"disambiguationData":[OSD([sQuery(id+"F6.wireOp",EDGE,"E14.3.0.1")])]})]});
            var Q116;
            Q116=makeQuery(id+"F7.boolean.opBoolean","INTERSECT",EDGE,{"derivedFrom":[makeQuery(id+"F3.opExtrude","SWEPT_FACE",FACE,{"disambiguationData":[OSD([sQuery(id+"F2.wireOp",EDGE,"E6.left")])]}),makeQuery(id+"F7.opExtrude","SWEPT_FACE",FACE,{"disambiguationData":[OSD([sQuery(id+"F6.wireOp",EDGE,"E14.4.0.1")])]})]});
            var Q117;
            Q117=makeQuery(id+"F7.boolean.opBoolean","INTERSECT",EDGE,{"derivedFrom":[makeQuery(id+"F3.opExtrude","SWEPT_FACE",FACE,{"disambiguationData":[OSD([sQuery(id+"F2.wireOp",EDGE,"E6.left")])]}),makeQuery(id+"F7.opExtrude","SWEPT_FACE",FACE,{"disambiguationData":[OSD([sQuery(id+"F6.wireOp",EDGE,"E14.2.0.1")])]})]});
            var Q118;
            {var subQ0=sQuery(id+"F2.wireOp",EDGE,"E6.left");Q118=makeQuery(id+"F7.boolean.opBoolean","SPLIT",EDGE,{"disambiguationData":[TD([makeQuery(id+"F7.opExtrude","SWEPT_FACE",FACE,{"disambiguationData":[OSD([sQuery(id+"F6.wireOp",EDGE,"E14.1.0.0")])]})])],"derivedFrom":makeQuery(id+"F3.opExtrude","CAP_EDGE",EDGE,{"disambiguationData":[OSD([subQ0])],"isStart":true})});}
            var Q119;
            Q119=makeQuery(id+"F7.boolean.opBoolean","INTERSECT",EDGE,{"derivedFrom":[makeQuery(id+"F3.opExtrude","SWEPT_FACE",FACE,{"disambiguationData":[OSD([sQuery(id+"F2.wireOp",EDGE,"E6.left")])]}),makeQuery(id+"F7.opExtrude","SWEPT_FACE",FACE,{"disambiguationData":[OSD([sQuery(id+"F6.wireOp",EDGE,"E14.1.0.1")])]})]});
            var Q120;
            {var subQ0=sQuery(id+"F2.wireOp",EDGE,"E6.left");Q120=makeQuery(id+"F7.boolean.opBoolean","SPLIT",EDGE,{"disambiguationData":[TD([makeQuery(id+"F7.opExtrude","SWEPT_FACE",FACE,{"disambiguationData":[OSD([sQuery(id+"F6.wireOp",EDGE,"E13")])]})])],"derivedFrom":makeQuery(id+"F3.opExtrude","CAP_EDGE",EDGE,{"disambiguationData":[OSD([subQ0])],"isStart":true})});}
            var Q121;
            Q121=makeQuery(id+"F7.boolean.opBoolean","INTERSECT",EDGE,{"derivedFrom":[makeQuery(id+"F3.opExtrude","SWEPT_FACE",FACE,{"disambiguationData":[OSD([sQuery(id+"F2.wireOp",EDGE,"E6.left")])]}),makeQuery(id+"F7.opExtrude","SWEPT_FACE",FACE,{"disambiguationData":[OSD([sQuery(id+"F6.wireOp",EDGE,"E12")])]})]});
            var Q122;
            {var subQ0=sQuery(id+"F2.wireOp",EDGE,"E6.left");var subQ1=sQuery(id+"F2.wireOp",EDGE,"E6.top");Q122=makeQuery(id+"F7.boolean.opBoolean","SPLIT",EDGE,{"disambiguationData":[TD([makeQuery(id+"F3.opExtrude","SWEPT_FACE",FACE,{"disambiguationData":[OSD([subQ1])]})])],"derivedFrom":makeQuery(id+"F3.opExtrude","CAP_EDGE",EDGE,{"disambiguationData":[OSD([subQ0])],"isStart":true})});}
            var Q123;
            Q123=makeQuery(id+"F1.opExtrude","SWEPT_EDGE",EDGE,{"disambiguationData":[OSD([sQuery(id+"F0.wireOp",EDGE,"E0.bottom"),sQuery(id+"F0.wireOp",EDGE,"E0.right")])]});
            var Q124;
            {var subQ0=sQuery(id+"F2.wireOp",EDGE,"E5.bottom");var subQ1=sQuery(id+"F2.wireOp",EDGE,"E5.left");Q124=makeQuery(id+"F7.boolean.opBoolean","SPLIT",EDGE,{"disambiguationData":[TD([makeQuery(id+"F3.opExtrude","SWEPT_FACE",FACE,{"disambiguationData":[OSD([subQ0])]})])],"derivedFrom":makeQuery(id+"F3.opExtrude","CAP_EDGE",EDGE,{"disambiguationData":[OSD([subQ1])],"isStart":true})});}
            var Q125;
            {var subQ0=sQuery(id+"F2.wireOp",EDGE,"E5.left");Q125=makeQuery(id+"F7.boolean.opBoolean","SPLIT",EDGE,{"disambiguationData":[TD([makeQuery(id+"F7.opExtrude","SWEPT_FACE",FACE,{"disambiguationData":[OSD([sQuery(id+"F6.wireOp",EDGE,"E14.3.0.0")])]})])],"derivedFrom":makeQuery(id+"F3.opExtrude","CAP_EDGE",EDGE,{"disambiguationData":[OSD([subQ0])],"isStart":true})});}
            var Q126;
            {var subQ0=sQuery(id+"F2.wireOp",EDGE,"E5.left");Q126=makeQuery(id+"F7.boolean.opBoolean","SPLIT",EDGE,{"disambiguationData":[TD([makeQuery(id+"F7.opExtrude","SWEPT_FACE",FACE,{"disambiguationData":[OSD([sQuery(id+"F6.wireOp",EDGE,"E14.2.0.0")])]})])],"derivedFrom":makeQuery(id+"F3.opExtrude","CAP_EDGE",EDGE,{"disambiguationData":[OSD([subQ0])],"isStart":true})});}
            var Q127;
            {var subQ0=sQuery(id+"F2.wireOp",EDGE,"E5.left");Q127=makeQuery(id+"F7.boolean.opBoolean","SPLIT",EDGE,{"disambiguationData":[TD([makeQuery(id+"F7.opExtrude","SWEPT_FACE",FACE,{"disambiguationData":[OSD([sQuery(id+"F6.wireOp",EDGE,"E14.1.0.0")])]})])],"derivedFrom":makeQuery(id+"F3.opExtrude","CAP_EDGE",EDGE,{"disambiguationData":[OSD([subQ0])],"isStart":true})});}
            var Q128;
            {var subQ0=sQuery(id+"F2.wireOp",EDGE,"E5.left");Q128=makeQuery(id+"F7.boolean.opBoolean","SPLIT",EDGE,{"disambiguationData":[TD([makeQuery(id+"F7.opExtrude","SWEPT_FACE",FACE,{"disambiguationData":[OSD([sQuery(id+"F6.wireOp",EDGE,"E13")])]})])],"derivedFrom":makeQuery(id+"F3.opExtrude","CAP_EDGE",EDGE,{"disambiguationData":[OSD([subQ0])],"isStart":true})});}
            var Q129;
            {var subQ0=sQuery(id+"F2.wireOp",EDGE,"E5.left");var subQ1=sQuery(id+"F2.wireOp",EDGE,"E5.top");Q129=makeQuery(id+"F7.boolean.opBoolean","SPLIT",EDGE,{"disambiguationData":[TD([makeQuery(id+"F3.opExtrude","SWEPT_FACE",FACE,{"disambiguationData":[OSD([subQ1])]})])],"derivedFrom":makeQuery(id+"F3.opExtrude","CAP_EDGE",EDGE,{"disambiguationData":[OSD([subQ0])],"isStart":true})});}
            var Q130;
            Q130=makeQuery(id+"F7.boolean.opBoolean","INTERSECT",EDGE,{"derivedFrom":[makeQuery(id+"F3.opExtrude","SWEPT_FACE",FACE,{"disambiguationData":[OSD([sQuery(id+"F2.wireOp",EDGE,"E5.left")])]}),makeQuery(id+"F7.opExtrude","SWEPT_FACE",FACE,{"disambiguationData":[OSD([sQuery(id+"F6.wireOp",EDGE,"E12")])]})]});
            var Q131;
            Q131=makeQuery(id+"F7.boolean.opBoolean","INTERSECT",EDGE,{"derivedFrom":[makeQuery(id+"F3.opExtrude","SWEPT_FACE",FACE,{"disambiguationData":[OSD([sQuery(id+"F2.wireOp",EDGE,"E5.left")])]}),makeQuery(id+"F7.opExtrude","SWEPT_FACE",FACE,{"disambiguationData":[OSD([sQuery(id+"F6.wireOp",EDGE,"E14.1.0.1")])]})]});
            var Q132;
            Q132=makeQuery(id+"F7.boolean.opBoolean","INTERSECT",EDGE,{"derivedFrom":[makeQuery(id+"F3.opExtrude","SWEPT_FACE",FACE,{"disambiguationData":[OSD([sQuery(id+"F2.wireOp",EDGE,"E5.left")])]}),makeQuery(id+"F7.opExtrude","SWEPT_FACE",FACE,{"disambiguationData":[OSD([sQuery(id+"F6.wireOp",EDGE,"E14.2.0.1")])]})]});
            var Q133;
            Q133=makeQuery(id+"F7.boolean.opBoolean","INTERSECT",EDGE,{"derivedFrom":[makeQuery(id+"F3.opExtrude","SWEPT_FACE",FACE,{"disambiguationData":[OSD([sQuery(id+"F2.wireOp",EDGE,"E5.left")])]}),makeQuery(id+"F7.opExtrude","SWEPT_FACE",FACE,{"disambiguationData":[OSD([sQuery(id+"F6.wireOp",EDGE,"E14.3.0.1")])]})]});
            var Q134;
            Q134=makeQuery(id+"F7.boolean.opBoolean","INTERSECT",EDGE,{"derivedFrom":[makeQuery(id+"F3.opExtrude","SWEPT_FACE",FACE,{"disambiguationData":[OSD([sQuery(id+"F2.wireOp",EDGE,"E5.left")])]}),makeQuery(id+"F7.opExtrude","SWEPT_FACE",FACE,{"disambiguationData":[OSD([sQuery(id+"F6.wireOp",EDGE,"E14.4.0.1")])]})]});
            var Q135;
            Q135=makeQuery(id+"F9.boolean.opBoolean","INTERSECT",EDGE,{"derivedFrom":[makeQuery(id+"F7.boolean.opBoolean","COPY",FACE,{"disambiguationData":[TD([makeQuery(id+"F3.opExtrude","SWEPT_FACE",FACE,{"disambiguationData":[OSD([sQuery(id+"F2.wireOp",EDGE,"E5.left")])]})])],"derivedFrom":makeQuery(id+"F7.opExtrude","SWEPT_FACE",FACE,{"disambiguationData":[OSD([sQuery(id+"F6.wireOp",EDGE,"E14.1.0.1")])]})}),makeQuery(id+"F9.opExtrude","SWEPT_FACE",FACE,{"disambiguationData":[OSD([sQuery(id+"F8.wireOp",EDGE,"E81.MirrorCS")])]})]});
            var Q136;
            Q136=makeQuery(id+"F9.boolean.opBoolean","INTERSECT",EDGE,{"derivedFrom":[makeQuery(id+"F7.boolean.opBoolean","COPY",FACE,{"disambiguationData":[TD([makeQuery(id+"F3.opExtrude","SWEPT_FACE",FACE,{"disambiguationData":[OSD([sQuery(id+"F2.wireOp",EDGE,"E5.left")])]})])],"derivedFrom":makeQuery(id+"F7.opExtrude","SWEPT_FACE",FACE,{"disambiguationData":[OSD([sQuery(id+"F6.wireOp",EDGE,"E12")])]})}),makeQuery(id+"F9.opExtrude","SWEPT_FACE",FACE,{"disambiguationData":[OSD([sQuery(id+"F8.wireOp",EDGE,"E89.MirrorCS")])]})]});
            var Q137;
            Q137=makeQuery(id+"F9.boolean.opBoolean","INTERSECT",EDGE,{"derivedFrom":[makeQuery(id+"F7.boolean.opBoolean","COPY",FACE,{"disambiguationData":[TD([makeQuery(id+"F3.opExtrude","SWEPT_FACE",FACE,{"disambiguationData":[OSD([sQuery(id+"F2.wireOp",EDGE,"E5.left")])]})])],"derivedFrom":makeQuery(id+"F7.opExtrude","SWEPT_FACE",FACE,{"disambiguationData":[OSD([sQuery(id+"F6.wireOp",EDGE,"E14.2.0.1")])]})}),makeQuery(id+"F9.opExtrude","SWEPT_FACE",FACE,{"disambiguationData":[OSD([sQuery(id+"F8.wireOp",EDGE,"E86.MirrorCS")])]})]});
            var Q138;
            Q138=makeQuery(id+"F9.boolean.opBoolean","INTERSECT",EDGE,{"derivedFrom":[makeQuery(id+"F7.boolean.opBoolean","COPY",FACE,{"disambiguationData":[TD([makeQuery(id+"F3.opExtrude","SWEPT_FACE",FACE,{"disambiguationData":[OSD([sQuery(id+"F2.wireOp",EDGE,"E5.left")])]})])],"derivedFrom":makeQuery(id+"F7.opExtrude","SWEPT_FACE",FACE,{"disambiguationData":[OSD([sQuery(id+"F6.wireOp",EDGE,"E14.3.0.1")])]})}),makeQuery(id+"F9.opExtrude","SWEPT_FACE",FACE,{"disambiguationData":[OSD([sQuery(id+"F8.wireOp",EDGE,"E80.MirrorCS")])]})]});
            var Q139;
            Q139=makeQuery(id+"F9.boolean.opBoolean","INTERSECT",EDGE,{"derivedFrom":[makeQuery(id+"F7.boolean.opBoolean","COPY",FACE,{"disambiguationData":[TD([makeQuery(id+"F3.opExtrude","SWEPT_FACE",FACE,{"disambiguationData":[OSD([sQuery(id+"F2.wireOp",EDGE,"E5.left")])]})])],"derivedFrom":makeQuery(id+"F7.opExtrude","SWEPT_FACE",FACE,{"disambiguationData":[OSD([sQuery(id+"F6.wireOp",EDGE,"E14.4.0.1")])]})}),makeQuery(id+"F9.opExtrude","SWEPT_FACE",FACE,{"disambiguationData":[OSD([sQuery(id+"F8.wireOp",EDGE,"E87.MirrorCS")])]})]});
            fillet(context, id + "F13", {"entities" : qUnion([Q0, Q1, Q2, Q3, Q4, Q5, Q6, Q7, Q8, Q9, Q10, Q11, Q12, Q13, Q14, Q15, Q16, Q17, Q18, Q19, Q20, Q21, Q22, Q23, Q24, Q25, Q26, Q27, Q28, Q29, Q30, Q31, Q32, Q33, Q34, Q35, Q36, Q37, Q38, Q39, Q40, Q41, Q42, Q43, Q44, Q45, Q46, Q47, Q48, Q49, Q50, Q51, Q52, Q53, Q54, Q55, Q56, Q57, Q58, Q59, Q60, Q61, Q62, Q63, Q64, Q65, Q66, Q67, Q68, Q69, Q70, Q71, Q72, Q73, Q74, Q75, Q76, Q77, Q78, Q79, Q80, Q81, Q82, Q83, Q84, Q85, Q86, Q87, Q88, Q89, Q90, Q91, Q92, Q93, Q94, Q95, Q96, Q97, Q98, Q99, Q100, Q101, Q102, Q103, Q104, Q105, Q106, Q107, Q108, Q109, Q110, Q111, Q112, Q113, Q114, Q115, Q116, Q117, Q118, Q119, Q120, Q121, Q122, Q123, Q124, Q125, Q126, Q127, Q128, Q129, Q130, Q131, Q132, Q133, Q134, Q135, Q136, Q137, Q138, Q139]), "radius" : 0.5 * mm, "tangentPropagation" : true, "allowEdgeOverflow" : false});
        }
        {
            var Q0;
            Q0=makeQuery(id+"F1.opExtrude","SWEPT_BODY",BODY,{"disambiguationData":[OSD([sQuery(id+"F0.wireOp",EDGE,"E0.bottom"),sQuery(id+"F0.wireOp",EDGE,"E0.top"),sQuery(id+"F0.wireOp",EDGE,"E0.left"),sQuery(id+"F0.wireOp",EDGE,"E0.right")])]});
            var Q1;
            Q1=makeQuery(id+"F1.opExtrude","SWEPT_BODY",BODY,{"disambiguationData":[OSD([sQuery(id+"F0.wireOp",EDGE,"E1.MirrorCS"),sQuery(id+"F0.wireOp",EDGE,"E2.MirrorCS"),sQuery(id+"F0.wireOp",EDGE,"E3.MirrorCS"),sQuery(id+"F0.wireOp",EDGE,"E4.MirrorCS")])]});
            var Q2;
            Q2=makeQuery(id+"F3.opExtrude","SWEPT_BODY",BODY,{"disambiguationData":[OSD([sQuery(id+"F2.wireOp",EDGE,"E6.bottom"),sQuery(id+"F2.wireOp",EDGE,"E6.top"),sQuery(id+"F2.wireOp",EDGE,"E6.left"),sQuery(id+"F2.wireOp",EDGE,"E6.right")])]});
            var Q3;
            Q3=makeQuery(id+"F3.opExtrude","SWEPT_BODY",BODY,{"disambiguationData":[OSD([sQuery(id+"F2.wireOp",EDGE,"E7.bottom"),sQuery(id+"F2.wireOp",EDGE,"E7.top"),sQuery(id+"F2.wireOp",EDGE,"E7.left"),sQuery(id+"F2.wireOp",EDGE,"E7.right")])]});
            var Q4;
            Q4=makeQuery(id+"F12.opExtrude","SWEPT_BODY",BODY,{"disambiguationData":[OSD([sQuery(id+"F11.wireOp",EDGE,"E90.0"),sQuery(id+"F11.wireOp",EDGE,"E90.1"),sQuery(id+"F11.wireOp",EDGE,"E90.2"),sQuery(id+"F11.wireOp",EDGE,"E90.3")])]});
            var Q5;
            Q5=makeQuery(id+"F12.opExtrude","SWEPT_BODY",BODY,{"disambiguationData":[OSD([sQuery(id+"F11.wireOp",EDGE,"E90.4"),sQuery(id+"F11.wireOp",EDGE,"E90.5"),sQuery(id+"F11.wireOp",EDGE,"E90.6"),sQuery(id+"F11.wireOp",EDGE,"E90.7")])]});
            deleteBodies(context, id + "F14", {"entities" : qUnion([Q0, Q1, Q2, Q3, Q4, Q5])});
        }
        {
            var Q0;
            Q0=makeQuery(id+"F3.opExtrude","CAP_EDGE",EDGE,{"disambiguationData":[OSD([sQuery(id+"F2.wireOp",EDGE,"E5.bottom")])],"isStart":true});
            var Q1;
            Q1=makeQuery(id+"F3.opExtrude","CAP_EDGE",EDGE,{"disambiguationData":[OSD([sQuery(id+"F2.wireOp",EDGE,"E5.top")])],"isStart":true});
            var Q2;
            Q2=makeQuery(id+"F9.boolean.opBoolean","MERGE",EDGE,{"derivedFrom":[makeQuery(id+"F7.boolean.opBoolean","COPY",EDGE,{"derivedFrom":makeQuery(id+"F7.opExtrude","CAP_EDGE",EDGE,{"disambiguationData":[OSD([sQuery(id+"F6.wireOp",EDGE,"E14.4.0.0")])],"isStart":true})}),makeQuery(id+"F7.boolean.opBoolean","COPY",EDGE,{"derivedFrom":makeQuery(id+"F7.opExtrude","CAP_EDGE",EDGE,{"disambiguationData":[OSD([sQuery(id+"F6.wireOp",EDGE,"E21.MirrorCS")])],"isStart":true})}),makeQuery(id+"F9.opExtrude","SWEPT_EDGE",EDGE,{"disambiguationData":[OSD([sQuery(id+"F8.wireOp",EDGE,"E42.bottom"),sQuery(id+"F8.wireOp",EDGE,"E42.right")])]})]});
            var Q3;
            Q3=makeQuery(id+"F9.boolean.opBoolean","MERGE",EDGE,{"derivedFrom":[makeQuery(id+"F7.boolean.opBoolean","COPY",EDGE,{"derivedFrom":makeQuery(id+"F7.opExtrude","CAP_EDGE",EDGE,{"disambiguationData":[OSD([sQuery(id+"F6.wireOp",EDGE,"E14.4.0.2")])],"isStart":true})}),makeQuery(id+"F7.boolean.opBoolean","COPY",EDGE,{"derivedFrom":makeQuery(id+"F7.opExtrude","CAP_EDGE",EDGE,{"disambiguationData":[OSD([sQuery(id+"F6.wireOp",EDGE,"E30.MirrorCS")])],"isStart":true})}),makeQuery(id+"F9.opExtrude","SWEPT_EDGE",EDGE,{"disambiguationData":[OSD([sQuery(id+"F8.wireOp",EDGE,"E42.top"),sQuery(id+"F8.wireOp",EDGE,"E42.right")])]})]});
            var Q4;
            Q4=makeQuery(id+"F9.boolean.opBoolean","MERGE",EDGE,{"derivedFrom":[makeQuery(id+"F7.boolean.opBoolean","COPY",EDGE,{"derivedFrom":makeQuery(id+"F7.opExtrude","CAP_EDGE",EDGE,{"disambiguationData":[OSD([sQuery(id+"F6.wireOp",EDGE,"E14.3.0.0")])],"isStart":true})}),makeQuery(id+"F7.boolean.opBoolean","COPY",EDGE,{"derivedFrom":makeQuery(id+"F7.opExtrude","CAP_EDGE",EDGE,{"disambiguationData":[OSD([sQuery(id+"F6.wireOp",EDGE,"E29.MirrorCS")])],"isStart":true})}),makeQuery(id+"F9.opExtrude","SWEPT_EDGE",EDGE,{"disambiguationData":[OSD([sQuery(id+"F8.wireOp",EDGE,"E43.0.1.1"),sQuery(id+"F8.wireOp",EDGE,"E43.0.1.2")])]})]});
            var Q5;
            Q5=makeQuery(id+"F9.boolean.opBoolean","MERGE",EDGE,{"derivedFrom":[makeQuery(id+"F7.boolean.opBoolean","COPY",EDGE,{"derivedFrom":makeQuery(id+"F7.opExtrude","CAP_EDGE",EDGE,{"disambiguationData":[OSD([sQuery(id+"F6.wireOp",EDGE,"E14.3.0.2")])],"isStart":true})}),makeQuery(id+"F7.boolean.opBoolean","COPY",EDGE,{"derivedFrom":makeQuery(id+"F7.opExtrude","CAP_EDGE",EDGE,{"disambiguationData":[OSD([sQuery(id+"F6.wireOp",EDGE,"E22.MirrorCS")])],"isStart":true})}),makeQuery(id+"F9.opExtrude","SWEPT_EDGE",EDGE,{"disambiguationData":[OSD([sQuery(id+"F8.wireOp",EDGE,"E43.0.1.0"),sQuery(id+"F8.wireOp",EDGE,"E43.0.1.2")])]})]});
            var Q6;
            Q6=makeQuery(id+"F9.boolean.opBoolean","MERGE",EDGE,{"derivedFrom":[makeQuery(id+"F7.boolean.opBoolean","COPY",EDGE,{"derivedFrom":makeQuery(id+"F7.opExtrude","CAP_EDGE",EDGE,{"disambiguationData":[OSD([sQuery(id+"F6.wireOp",EDGE,"E14.2.0.0")])],"isStart":true})}),makeQuery(id+"F7.boolean.opBoolean","COPY",EDGE,{"derivedFrom":makeQuery(id+"F7.opExtrude","CAP_EDGE",EDGE,{"disambiguationData":[OSD([sQuery(id+"F6.wireOp",EDGE,"E27.MirrorCS")])],"isStart":true})}),makeQuery(id+"F9.opExtrude","SWEPT_EDGE",EDGE,{"disambiguationData":[OSD([sQuery(id+"F8.wireOp",EDGE,"E43.0.2.1"),sQuery(id+"F8.wireOp",EDGE,"E43.0.2.2")])]})]});
            var Q7;
            Q7=makeQuery(id+"F9.boolean.opBoolean","MERGE",EDGE,{"derivedFrom":[makeQuery(id+"F7.boolean.opBoolean","COPY",EDGE,{"derivedFrom":makeQuery(id+"F7.opExtrude","CAP_EDGE",EDGE,{"disambiguationData":[OSD([sQuery(id+"F6.wireOp",EDGE,"E14.2.0.2")])],"isStart":true})}),makeQuery(id+"F7.boolean.opBoolean","COPY",EDGE,{"derivedFrom":makeQuery(id+"F7.opExtrude","CAP_EDGE",EDGE,{"disambiguationData":[OSD([sQuery(id+"F6.wireOp",EDGE,"E28.MirrorCS")])],"isStart":true})}),makeQuery(id+"F9.opExtrude","SWEPT_EDGE",EDGE,{"disambiguationData":[OSD([sQuery(id+"F8.wireOp",EDGE,"E43.0.2.0"),sQuery(id+"F8.wireOp",EDGE,"E43.0.2.2")])]})]});
            var Q8;
            Q8=makeQuery(id+"F9.boolean.opBoolean","MERGE",EDGE,{"derivedFrom":[makeQuery(id+"F7.boolean.opBoolean","COPY",EDGE,{"derivedFrom":makeQuery(id+"F7.opExtrude","CAP_EDGE",EDGE,{"disambiguationData":[OSD([sQuery(id+"F6.wireOp",EDGE,"E14.1.0.0")])],"isStart":true})}),makeQuery(id+"F7.boolean.opBoolean","COPY",EDGE,{"derivedFrom":makeQuery(id+"F7.opExtrude","CAP_EDGE",EDGE,{"disambiguationData":[OSD([sQuery(id+"F6.wireOp",EDGE,"E25.MirrorCS")])],"isStart":true})}),makeQuery(id+"F9.opExtrude","SWEPT_EDGE",EDGE,{"disambiguationData":[OSD([sQuery(id+"F8.wireOp",EDGE,"E43.0.3.1"),sQuery(id+"F8.wireOp",EDGE,"E43.0.3.2")])]})]});
            var Q9;
            Q9=makeQuery(id+"F9.boolean.opBoolean","MERGE",EDGE,{"derivedFrom":[makeQuery(id+"F7.boolean.opBoolean","COPY",EDGE,{"derivedFrom":makeQuery(id+"F7.opExtrude","CAP_EDGE",EDGE,{"disambiguationData":[OSD([sQuery(id+"F6.wireOp",EDGE,"E14.1.0.2")])],"isStart":true})}),makeQuery(id+"F7.boolean.opBoolean","COPY",EDGE,{"derivedFrom":makeQuery(id+"F7.opExtrude","CAP_EDGE",EDGE,{"disambiguationData":[OSD([sQuery(id+"F6.wireOp",EDGE,"E26.MirrorCS")])],"isStart":true})}),makeQuery(id+"F9.opExtrude","SWEPT_EDGE",EDGE,{"disambiguationData":[OSD([sQuery(id+"F8.wireOp",EDGE,"E43.0.3.0"),sQuery(id+"F8.wireOp",EDGE,"E43.0.3.2")])]})]});
            var Q10;
            Q10=makeQuery(id+"F9.boolean.opBoolean","MERGE",EDGE,{"derivedFrom":[makeQuery(id+"F7.boolean.opBoolean","COPY",EDGE,{"derivedFrom":makeQuery(id+"F7.opExtrude","CAP_EDGE",EDGE,{"disambiguationData":[OSD([sQuery(id+"F6.wireOp",EDGE,"E13")])],"isStart":true})}),makeQuery(id+"F7.boolean.opBoolean","COPY",EDGE,{"derivedFrom":makeQuery(id+"F7.opExtrude","CAP_EDGE",EDGE,{"disambiguationData":[OSD([sQuery(id+"F6.wireOp",EDGE,"E24.MirrorCS")])],"isStart":true})}),makeQuery(id+"F9.opExtrude","SWEPT_EDGE",EDGE,{"disambiguationData":[OSD([sQuery(id+"F8.wireOp",EDGE,"E43.0.4.1"),sQuery(id+"F8.wireOp",EDGE,"E43.0.4.2")])]})]});
            var Q11;
            Q11=makeQuery(id+"F9.boolean.opBoolean","MERGE",EDGE,{"derivedFrom":[makeQuery(id+"F7.boolean.opBoolean","COPY",EDGE,{"derivedFrom":makeQuery(id+"F7.opExtrude","CAP_EDGE",EDGE,{"disambiguationData":[OSD([sQuery(id+"F6.wireOp",EDGE,"E11")])],"isStart":true})}),makeQuery(id+"F7.boolean.opBoolean","COPY",EDGE,{"derivedFrom":makeQuery(id+"F7.opExtrude","CAP_EDGE",EDGE,{"disambiguationData":[OSD([sQuery(id+"F6.wireOp",EDGE,"E23.MirrorCS")])],"isStart":true})}),makeQuery(id+"F9.opExtrude","SWEPT_EDGE",EDGE,{"disambiguationData":[OSD([sQuery(id+"F2.wireOp",EDGE,"E5.right"),sQuery(id+"F8.wireOp",EDGE,"E43.0.4.0"),sQuery(id+"F8.wireOp",EDGE,"E43.0.4.2")])]})]});
            fillet(context, id + "F15", {"entities" : qUnion([Q0, Q1, Q2, Q3, Q4, Q5, Q6, Q7, Q8, Q9, Q10, Q11]), "radius" : 0.5 * mm, "tangentPropagation" : true, "allowEdgeOverflow" : false});
        }
    });
